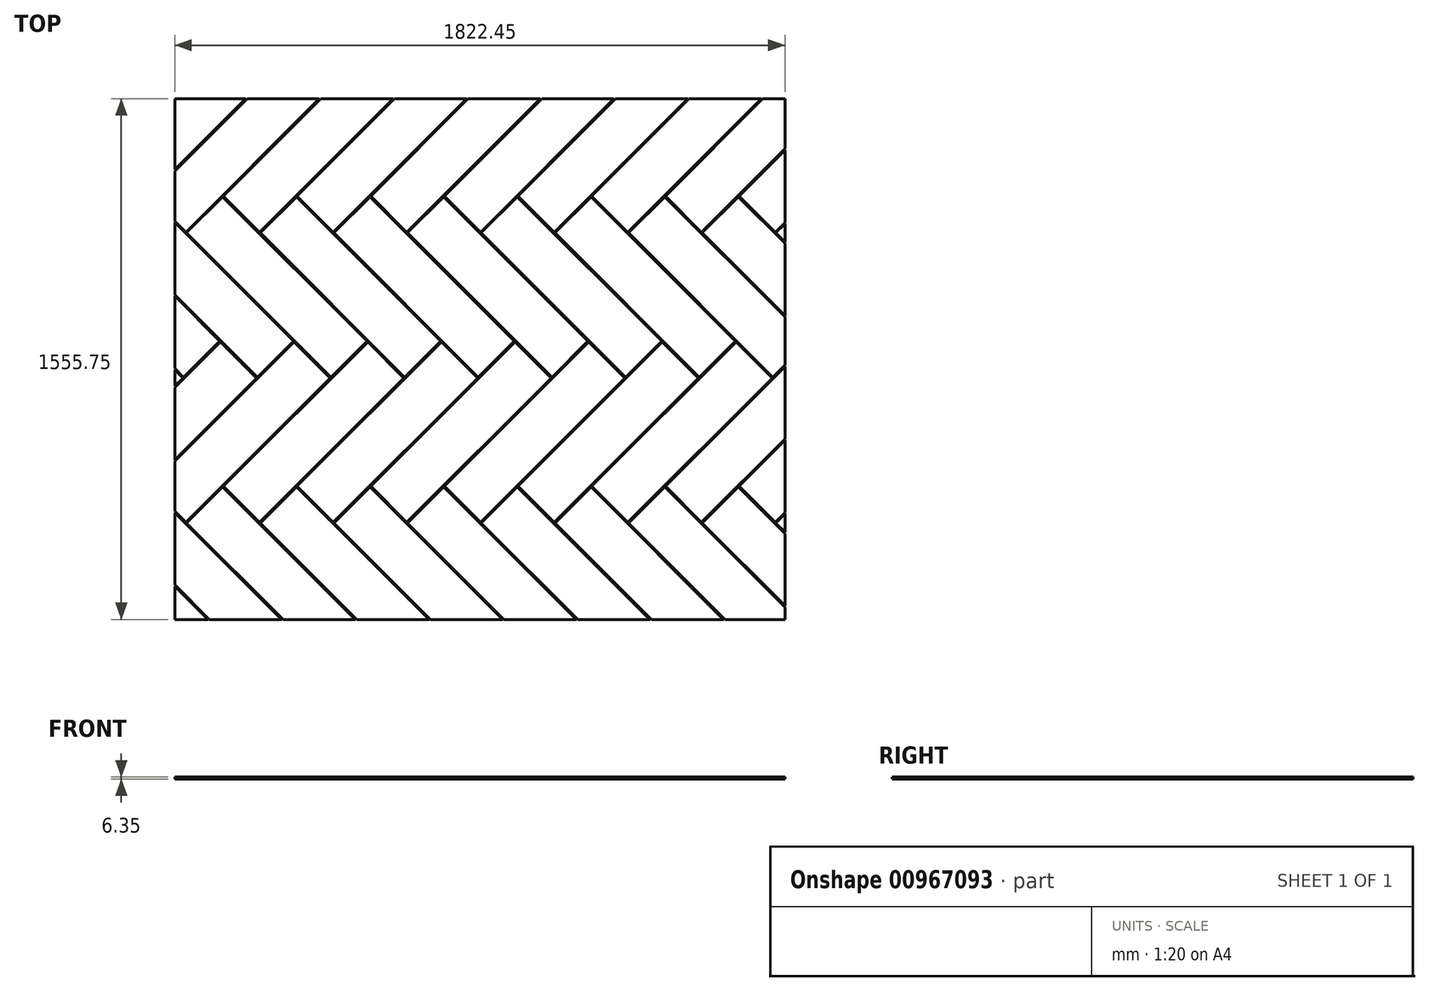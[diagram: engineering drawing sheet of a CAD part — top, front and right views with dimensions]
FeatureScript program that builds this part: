
annotation { "Feature Type Name" : "Feature", "Feature Type Description" : "" }
export const myFeature = defineFeature(function(context is Context, id is Id, definition is map)
    precondition{}
    {
        {
            var Q0;
            Q0=qCreatedBy(makeId("Top.planeOp"),FACE);
            var sketch = newSketch(context, id + "F0", { "sketchPlane" : qUnion([Q0])});
            skLineSegment(sketch, "E0.bottom", {"start": v(0, 0) * mm, "end": v(609.6, 0) * mm});
            skLineSegment(sketch, "E0.top", {"start": v(0, 152.4) * mm, "end": v(609.6, 152.4) * mm});
            skLineSegment(sketch, "E0.left", {"start": v(0, 0) * mm, "end": v(0, 152.4) * mm});
            skLineSegment(sketch, "E0.right", {"start": v(609.6, 0) * mm, "end": v(609.6, 152.4) * mm});
            skLineSegment(sketch, "E1.bottom", {"start": v(152.4, 155.57) * mm, "end": v(152.4, 765.17) * mm});
            skLineSegment(sketch, "E1.top", {"start": v(0, 155.58) * mm, "end": v(0, 765.17) * mm});
            skLineSegment(sketch, "E1.left", {"start": v(152.4, 155.57) * mm, "end": v(0, 155.57) * mm});
            skLineSegment(sketch, "E1.right", {"start": v(152.4, 765.17) * mm, "end": v(0, 765.17) * mm});
            skLineSegment(sketch, "E2.bottom", {"start": v(155.58, 155.57) * mm, "end": v(765.17, 155.57) * mm});
            skLineSegment(sketch, "E2.top", {"start": v(155.58, 307.98) * mm, "end": v(765.17, 307.97) * mm});
            skLineSegment(sketch, "E2.left", {"start": v(155.58, 155.58) * mm, "end": v(155.58, 307.98) * mm});
            skLineSegment(sketch, "E2.right", {"start": v(765.17, 155.57) * mm, "end": v(765.17, 307.97) * mm});
            skLineSegment(sketch, "E3.bottom", {"start": v(307.98, 311.15) * mm, "end": v(307.98, 920.75) * mm});
            skLineSegment(sketch, "E3.top", {"start": v(155.58, 311.15) * mm, "end": v(155.58, 920.75) * mm});
            skLineSegment(sketch, "E3.left", {"start": v(307.98, 311.15) * mm, "end": v(155.58, 311.15) * mm});
            skLineSegment(sketch, "E3.right", {"start": v(307.98, 920.75) * mm, "end": v(155.58, 920.75) * mm});
            skLineSegment(sketch, "E4.0.1.0", {"start": v(-612.78, 612.78) * mm, "end": v(-3.18, 612.78) * mm});
            skLineSegment(sketch, "E4.0.1.1", {"start": v(-460.37, 768.35) * mm, "end": v(-612.77, 768.35) * mm});
            skLineSegment(sketch, "E4.0.1.2", {"start": v(-457.2, 768.35) * mm, "end": v(-457.2, 920.75) * mm});
            skLineSegment(sketch, "E4.0.1.3", {"start": v(-304.8, 923.92) * mm, "end": v(-457.2, 923.92) * mm});
            skLineSegment(sketch, "E4.0.1.4", {"start": v(-457.2, 768.35) * mm, "end": v(152.4, 768.35) * mm});
            skLineSegment(sketch, "E4.0.1.5", {"start": v(-460.37, 768.35) * mm, "end": v(-460.37, 1377.95) * mm});
            skLineSegment(sketch, "E4.0.1.6", {"start": v(-457.2, 920.75) * mm, "end": v(152.4, 920.75) * mm});
            skLineSegment(sketch, "E4.0.1.7", {"start": v(-304.8, 1533.52) * mm, "end": v(-457.2, 1533.52) * mm});
            skLineSegment(sketch, "E4.0.1.8", {"start": v(-612.78, 768.35) * mm, "end": v(-612.77, 1377.95) * mm});
            skLineSegment(sketch, "E4.0.1.9", {"start": v(-457.2, 923.92) * mm, "end": v(-457.2, 1533.52) * mm});
            skLineSegment(sketch, "E4.0.1.10", {"start": v(-3.18, 612.78) * mm, "end": v(-3.18, 765.17) * mm});
            skLineSegment(sketch, "E4.0.1.11", {"start": v(-304.8, 923.92) * mm, "end": v(-304.8, 1533.52) * mm});
            skLineSegment(sketch, "E4.0.1.12", {"start": v(-612.78, 612.78) * mm, "end": v(-612.78, 765.17) * mm});
            skLineSegment(sketch, "E4.0.1.13", {"start": v(-460.37, 1377.95) * mm, "end": v(-612.77, 1377.95) * mm});
            skLineSegment(sketch, "E4.0.1.14", {"start": v(152.4, 768.35) * mm, "end": v(152.4, 920.75) * mm});
            skLineSegment(sketch, "E4.0.1.15", {"start": v(-612.77, 765.17) * mm, "end": v(-3.17, 765.17) * mm});
            skLineSegment(sketch, "E4.1.0.0", {"start": v(311.15, 311.15) * mm, "end": v(920.75, 311.15) * mm});
            skLineSegment(sketch, "E4.1.0.1", {"start": v(463.55, 466.72) * mm, "end": v(311.15, 466.72) * mm});
            skLineSegment(sketch, "E4.1.0.2", {"start": v(466.73, 466.72) * mm, "end": v(466.73, 619.12) * mm});
            skLineSegment(sketch, "E4.1.0.3", {"start": v(619.13, 622.3) * mm, "end": v(466.73, 622.3) * mm});
            skLineSegment(sketch, "E4.1.0.4", {"start": v(466.73, 466.72) * mm, "end": v(1076.33, 466.72) * mm});
            skLineSegment(sketch, "E4.1.0.5", {"start": v(463.55, 466.72) * mm, "end": v(463.55, 1076.32) * mm});
            skLineSegment(sketch, "E4.1.0.6", {"start": v(466.73, 619.12) * mm, "end": v(1076.33, 619.12) * mm});
            skLineSegment(sketch, "E4.1.0.7", {"start": v(619.13, 1231.9) * mm, "end": v(466.73, 1231.9) * mm});
            skLineSegment(sketch, "E4.1.0.8", {"start": v(311.15, 466.72) * mm, "end": v(311.15, 1076.32) * mm});
            skLineSegment(sketch, "E4.1.0.9", {"start": v(466.73, 622.3) * mm, "end": v(466.73, 1231.9) * mm});
            skLineSegment(sketch, "E4.1.0.10", {"start": v(920.75, 311.15) * mm, "end": v(920.75, 463.55) * mm});
            skLineSegment(sketch, "E4.1.0.11", {"start": v(619.13, 622.3) * mm, "end": v(619.13, 1231.9) * mm});
            skLineSegment(sketch, "E4.1.0.12", {"start": v(311.15, 311.15) * mm, "end": v(311.15, 463.55) * mm});
            skLineSegment(sketch, "E4.1.0.13", {"start": v(463.55, 1076.32) * mm, "end": v(311.15, 1076.32) * mm});
            skLineSegment(sketch, "E4.1.0.14", {"start": v(1076.32, 466.72) * mm, "end": v(1076.32, 619.12) * mm});
            skLineSegment(sketch, "E4.1.0.15", {"start": v(311.15, 463.55) * mm, "end": v(920.75, 463.55) * mm});
            skLineSegment(sketch, "E4.1.1.0", {"start": v(-301.62, 923.92) * mm, "end": v(307.98, 923.92) * mm});
            skLineSegment(sketch, "E4.1.1.1", {"start": v(-149.22, 1079.5) * mm, "end": v(-301.62, 1079.5) * mm});
            skLineSegment(sketch, "E4.1.1.2", {"start": v(-146.05, 1079.5) * mm, "end": v(-146.05, 1231.9) * mm});
            skLineSegment(sketch, "E4.1.1.3", {"start": v(6.35, 1235.07) * mm, "end": v(-146.05, 1235.07) * mm});
            skLineSegment(sketch, "E4.1.1.4", {"start": v(-146.05, 1079.5) * mm, "end": v(463.55, 1079.5) * mm});
            skLineSegment(sketch, "E4.1.1.5", {"start": v(-149.22, 1079.5) * mm, "end": v(-149.22, 1689.1) * mm});
            skLineSegment(sketch, "E4.1.1.6", {"start": v(-146.05, 1231.9) * mm, "end": v(463.55, 1231.9) * mm});
            skLineSegment(sketch, "E4.1.1.7", {"start": v(6.35, 1844.67) * mm, "end": v(-146.05, 1844.67) * mm});
            skLineSegment(sketch, "E4.1.1.8", {"start": v(-301.62, 1079.5) * mm, "end": v(-301.62, 1689.1) * mm});
            skLineSegment(sketch, "E4.1.1.9", {"start": v(-146.05, 1235.07) * mm, "end": v(-146.05, 1844.67) * mm});
            skLineSegment(sketch, "E4.1.1.10", {"start": v(307.98, 923.92) * mm, "end": v(307.98, 1076.32) * mm});
            skLineSegment(sketch, "E4.1.1.11", {"start": v(6.35, 1235.07) * mm, "end": v(6.35, 1844.67) * mm});
            skLineSegment(sketch, "E4.1.1.12", {"start": v(-301.62, 923.92) * mm, "end": v(-301.62, 1076.32) * mm});
            skLineSegment(sketch, "E4.1.1.13", {"start": v(-149.22, 1689.1) * mm, "end": v(-301.62, 1689.1) * mm});
            skLineSegment(sketch, "E4.1.1.14", {"start": v(463.55, 1079.5) * mm, "end": v(463.55, 1231.9) * mm});
            skLineSegment(sketch, "E4.1.1.15", {"start": v(-301.62, 1076.32) * mm, "end": v(307.98, 1076.32) * mm});
            skLineSegment(sketch, "E4.2.0.0", {"start": v(622.3, 622.3) * mm, "end": v(1231.9, 622.3) * mm});
            skLineSegment(sketch, "E4.2.0.1", {"start": v(774.7, 777.87) * mm, "end": v(622.3, 777.87) * mm});
            skLineSegment(sketch, "E4.2.0.2", {"start": v(777.88, 777.87) * mm, "end": v(777.88, 930.27) * mm});
            skLineSegment(sketch, "E4.2.0.3", {"start": v(930.28, 933.45) * mm, "end": v(777.88, 933.45) * mm});
            skLineSegment(sketch, "E4.2.0.4", {"start": v(777.88, 777.87) * mm, "end": v(1387.47, 777.87) * mm});
            skLineSegment(sketch, "E4.2.0.5", {"start": v(774.7, 777.87) * mm, "end": v(774.7, 1387.47) * mm});
            skLineSegment(sketch, "E4.2.0.6", {"start": v(777.88, 930.27) * mm, "end": v(1387.47, 930.27) * mm});
            skLineSegment(sketch, "E4.2.0.7", {"start": v(930.28, 1543.05) * mm, "end": v(777.88, 1543.05) * mm});
            skLineSegment(sketch, "E4.2.0.8", {"start": v(622.3, 777.87) * mm, "end": v(622.3, 1387.47) * mm});
            skLineSegment(sketch, "E4.2.0.9", {"start": v(777.88, 933.45) * mm, "end": v(777.88, 1543.05) * mm});
            skLineSegment(sketch, "E4.2.0.10", {"start": v(1231.9, 622.3) * mm, "end": v(1231.9, 774.7) * mm});
            skLineSegment(sketch, "E4.2.0.11", {"start": v(930.28, 933.45) * mm, "end": v(930.28, 1543.05) * mm});
            skLineSegment(sketch, "E4.2.0.12", {"start": v(622.3, 622.3) * mm, "end": v(622.3, 774.7) * mm});
            skLineSegment(sketch, "E4.2.0.13", {"start": v(774.7, 1387.47) * mm, "end": v(622.3, 1387.47) * mm});
            skLineSegment(sketch, "E4.2.0.14", {"start": v(1387.47, 777.87) * mm, "end": v(1387.47, 930.27) * mm});
            skLineSegment(sketch, "E4.2.0.15", {"start": v(622.3, 774.7) * mm, "end": v(1231.9, 774.7) * mm});
            skLineSegment(sketch, "E4.2.1.0", {"start": v(9.53, 1235.07) * mm, "end": v(619.13, 1235.07) * mm});
            skLineSegment(sketch, "E4.2.1.1", {"start": v(161.93, 1390.65) * mm, "end": v(9.53, 1390.65) * mm});
            skLineSegment(sketch, "E4.2.1.2", {"start": v(165.1, 1390.65) * mm, "end": v(165.1, 1543.05) * mm});
            skLineSegment(sketch, "E4.2.1.3", {"start": v(317.5, 1546.22) * mm, "end": v(165.1, 1546.22) * mm});
            skLineSegment(sketch, "E4.2.1.4", {"start": v(165.1, 1390.65) * mm, "end": v(774.7, 1390.65) * mm});
            skLineSegment(sketch, "E4.2.1.5", {"start": v(161.93, 1390.65) * mm, "end": v(161.93, 2000.25) * mm});
            skLineSegment(sketch, "E4.2.1.6", {"start": v(165.1, 1543.05) * mm, "end": v(774.7, 1543.05) * mm});
            skLineSegment(sketch, "E4.2.1.7", {"start": v(317.5, 2155.82) * mm, "end": v(165.1, 2155.82) * mm});
            skLineSegment(sketch, "E4.2.1.8", {"start": v(9.53, 1390.65) * mm, "end": v(9.53, 2000.25) * mm});
            skLineSegment(sketch, "E4.2.1.9", {"start": v(165.1, 1546.22) * mm, "end": v(165.1, 2155.82) * mm});
            skLineSegment(sketch, "E4.2.1.10", {"start": v(619.13, 1235.07) * mm, "end": v(619.13, 1387.47) * mm});
            skLineSegment(sketch, "E4.2.1.11", {"start": v(317.5, 1546.22) * mm, "end": v(317.5, 2155.82) * mm});
            skLineSegment(sketch, "E4.2.1.12", {"start": v(9.53, 1235.07) * mm, "end": v(9.53, 1387.47) * mm});
            skLineSegment(sketch, "E4.2.1.13", {"start": v(161.93, 2000.25) * mm, "end": v(9.53, 2000.25) * mm});
            skLineSegment(sketch, "E4.2.1.14", {"start": v(774.7, 1390.65) * mm, "end": v(774.7, 1543.05) * mm});
            skLineSegment(sketch, "E4.2.1.15", {"start": v(9.53, 1387.47) * mm, "end": v(619.13, 1387.47) * mm});
            skLineSegment(sketch, "E4.direction1", {"start": v(0, 0) * mm, "end": v(311.15, 311.15) * mm, "construction": true});
            skLineSegment(sketch, "E4.direction2", {"start": v(0, 0) * mm, "end": v(-612.78, 612.78) * mm, "construction": true});
            skLineSegment(sketch, "E5.0.3.0", {"start": v(933.45, 933.45) * mm, "end": v(1543.05, 933.45) * mm});
            skLineSegment(sketch, "E5.3.3.0", {"start": v(1085.85, 1089.02) * mm, "end": v(933.45, 1089.02) * mm});
            skLineSegment(sketch, "E5.6.3.0", {"start": v(1089.03, 1089.02) * mm, "end": v(1089.03, 1241.42) * mm});
            skLineSegment(sketch, "E5.9.3.0", {"start": v(1241.43, 1244.6) * mm, "end": v(1089.03, 1244.6) * mm});
            skLineSegment(sketch, "E5.12.3.0", {"start": v(1089.03, 1089.02) * mm, "end": v(1698.62, 1089.02) * mm});
            skLineSegment(sketch, "E5.15.3.0", {"start": v(1085.85, 1089.02) * mm, "end": v(1085.85, 1698.62) * mm});
            skLineSegment(sketch, "E5.18.3.0", {"start": v(1089.03, 1241.42) * mm, "end": v(1698.62, 1241.42) * mm});
            skLineSegment(sketch, "E5.21.3.0", {"start": v(1241.43, 1854.2) * mm, "end": v(1089.03, 1854.2) * mm});
            skLineSegment(sketch, "E5.24.3.0", {"start": v(933.45, 1089.02) * mm, "end": v(933.45, 1698.62) * mm});
            skLineSegment(sketch, "E5.27.3.0", {"start": v(1089.03, 1244.6) * mm, "end": v(1089.03, 1854.2) * mm});
            skLineSegment(sketch, "E5.30.3.0", {"start": v(1543.05, 933.45) * mm, "end": v(1543.05, 1085.85) * mm});
            skLineSegment(sketch, "E5.33.3.0", {"start": v(1241.43, 1244.6) * mm, "end": v(1241.43, 1854.2) * mm});
            skLineSegment(sketch, "E5.36.3.0", {"start": v(933.45, 933.45) * mm, "end": v(933.45, 1085.85) * mm});
            skLineSegment(sketch, "E5.39.3.0", {"start": v(1085.85, 1698.62) * mm, "end": v(933.45, 1698.62) * mm});
            skLineSegment(sketch, "E5.42.3.0", {"start": v(1698.62, 1089.02) * mm, "end": v(1698.62, 1241.42) * mm});
            skLineSegment(sketch, "E5.45.3.0", {"start": v(933.45, 1085.85) * mm, "end": v(1543.05, 1085.85) * mm});
            skLineSegment(sketch, "E5.0.3.1", {"start": v(320.68, 1546.22) * mm, "end": v(930.28, 1546.22) * mm});
            skLineSegment(sketch, "E5.3.3.1", {"start": v(473.08, 1701.8) * mm, "end": v(320.68, 1701.8) * mm});
            skLineSegment(sketch, "E5.6.3.1", {"start": v(476.25, 1701.8) * mm, "end": v(476.25, 1854.2) * mm});
            skLineSegment(sketch, "E5.9.3.1", {"start": v(628.65, 1857.37) * mm, "end": v(476.25, 1857.37) * mm});
            skLineSegment(sketch, "E5.12.3.1", {"start": v(476.25, 1701.8) * mm, "end": v(1085.85, 1701.8) * mm});
            skLineSegment(sketch, "E5.15.3.1", {"start": v(473.08, 1701.8) * mm, "end": v(473.08, 2311.4) * mm});
            skLineSegment(sketch, "E5.18.3.1", {"start": v(476.25, 1854.2) * mm, "end": v(1085.85, 1854.2) * mm});
            skLineSegment(sketch, "E5.21.3.1", {"start": v(628.65, 2466.97) * mm, "end": v(476.25, 2466.97) * mm});
            skLineSegment(sketch, "E5.24.3.1", {"start": v(320.68, 1701.8) * mm, "end": v(320.68, 2311.4) * mm});
            skLineSegment(sketch, "E5.27.3.1", {"start": v(476.25, 1857.37) * mm, "end": v(476.25, 2466.97) * mm});
            skLineSegment(sketch, "E5.30.3.1", {"start": v(930.28, 1546.22) * mm, "end": v(930.28, 1698.62) * mm});
            skLineSegment(sketch, "E5.33.3.1", {"start": v(628.65, 1857.37) * mm, "end": v(628.65, 2466.97) * mm});
            skLineSegment(sketch, "E5.36.3.1", {"start": v(320.68, 1546.22) * mm, "end": v(320.68, 1698.62) * mm});
            skLineSegment(sketch, "E5.39.3.1", {"start": v(473.08, 2311.4) * mm, "end": v(320.68, 2311.4) * mm});
            skLineSegment(sketch, "E5.42.3.1", {"start": v(1085.85, 1701.8) * mm, "end": v(1085.85, 1854.2) * mm});
            skLineSegment(sketch, "E5.45.3.1", {"start": v(320.68, 1698.62) * mm, "end": v(930.28, 1698.62) * mm});
            skLineSegment(sketch, "E5.0.4.0", {"start": v(1244.6, 1244.6) * mm, "end": v(1854.2, 1244.6) * mm});
            skLineSegment(sketch, "E5.3.4.0", {"start": v(1397, 1400.17) * mm, "end": v(1244.6, 1400.17) * mm});
            skLineSegment(sketch, "E5.6.4.0", {"start": v(1400.18, 1400.17) * mm, "end": v(1400.18, 1552.57) * mm});
            skLineSegment(sketch, "E5.9.4.0", {"start": v(1552.58, 1555.75) * mm, "end": v(1400.18, 1555.75) * mm});
            skLineSegment(sketch, "E5.12.4.0", {"start": v(1400.18, 1400.17) * mm, "end": v(2009.78, 1400.17) * mm});
            skLineSegment(sketch, "E5.15.4.0", {"start": v(1397, 1400.17) * mm, "end": v(1397, 2009.77) * mm});
            skLineSegment(sketch, "E5.18.4.0", {"start": v(1400.18, 1552.57) * mm, "end": v(2009.78, 1552.57) * mm});
            skLineSegment(sketch, "E5.21.4.0", {"start": v(1552.58, 2165.35) * mm, "end": v(1400.18, 2165.35) * mm});
            skLineSegment(sketch, "E5.24.4.0", {"start": v(1244.6, 1400.17) * mm, "end": v(1244.6, 2009.77) * mm});
            skLineSegment(sketch, "E5.27.4.0", {"start": v(1400.18, 1555.75) * mm, "end": v(1400.18, 2165.35) * mm});
            skLineSegment(sketch, "E5.30.4.0", {"start": v(1854.2, 1244.6) * mm, "end": v(1854.2, 1397) * mm});
            skLineSegment(sketch, "E5.33.4.0", {"start": v(1552.58, 1555.75) * mm, "end": v(1552.58, 2165.35) * mm});
            skLineSegment(sketch, "E5.36.4.0", {"start": v(1244.6, 1244.6) * mm, "end": v(1244.6, 1397) * mm});
            skLineSegment(sketch, "E5.39.4.0", {"start": v(1397, 2009.77) * mm, "end": v(1244.6, 2009.77) * mm});
            skLineSegment(sketch, "E5.42.4.0", {"start": v(2009.78, 1400.17) * mm, "end": v(2009.78, 1552.57) * mm});
            skLineSegment(sketch, "E5.45.4.0", {"start": v(1244.6, 1397) * mm, "end": v(1854.2, 1397) * mm});
            skLineSegment(sketch, "E5.0.4.1", {"start": v(631.83, 1857.37) * mm, "end": v(1241.43, 1857.37) * mm});
            skLineSegment(sketch, "E5.3.4.1", {"start": v(784.23, 2012.95) * mm, "end": v(631.83, 2012.95) * mm});
            skLineSegment(sketch, "E5.6.4.1", {"start": v(787.4, 2012.95) * mm, "end": v(787.4, 2165.35) * mm});
            skLineSegment(sketch, "E5.9.4.1", {"start": v(939.8, 2168.52) * mm, "end": v(787.4, 2168.52) * mm});
            skLineSegment(sketch, "E5.12.4.1", {"start": v(787.4, 2012.95) * mm, "end": v(1397, 2012.95) * mm});
            skLineSegment(sketch, "E5.15.4.1", {"start": v(784.23, 2012.95) * mm, "end": v(784.23, 2622.55) * mm});
            skLineSegment(sketch, "E5.18.4.1", {"start": v(787.4, 2165.35) * mm, "end": v(1397, 2165.35) * mm});
            skLineSegment(sketch, "E5.21.4.1", {"start": v(939.8, 2778.12) * mm, "end": v(787.4, 2778.12) * mm});
            skLineSegment(sketch, "E5.24.4.1", {"start": v(631.83, 2012.95) * mm, "end": v(631.83, 2622.55) * mm});
            skLineSegment(sketch, "E5.27.4.1", {"start": v(787.4, 2168.52) * mm, "end": v(787.4, 2778.12) * mm});
            skLineSegment(sketch, "E5.30.4.1", {"start": v(1241.43, 1857.37) * mm, "end": v(1241.43, 2009.77) * mm});
            skLineSegment(sketch, "E5.33.4.1", {"start": v(939.8, 2168.52) * mm, "end": v(939.8, 2778.12) * mm});
            skLineSegment(sketch, "E5.36.4.1", {"start": v(631.83, 1857.37) * mm, "end": v(631.83, 2009.77) * mm});
            skLineSegment(sketch, "E5.39.4.1", {"start": v(784.23, 2622.55) * mm, "end": v(631.83, 2622.55) * mm});
            skLineSegment(sketch, "E5.42.4.1", {"start": v(1397, 2012.95) * mm, "end": v(1397, 2165.35) * mm});
            skLineSegment(sketch, "E5.45.4.1", {"start": v(631.83, 2009.77) * mm, "end": v(1241.43, 2009.77) * mm});
            skLineSegment(sketch, "E5.0.5.0", {"start": v(1555.75, 1555.75) * mm, "end": v(2165.35, 1555.75) * mm});
            skLineSegment(sketch, "E5.3.5.0", {"start": v(1708.15, 1711.32) * mm, "end": v(1555.75, 1711.32) * mm});
            skLineSegment(sketch, "E5.6.5.0", {"start": v(1711.33, 1711.32) * mm, "end": v(1711.33, 1863.72) * mm});
            skLineSegment(sketch, "E5.9.5.0", {"start": v(1863.73, 1866.9) * mm, "end": v(1711.33, 1866.9) * mm});
            skLineSegment(sketch, "E5.12.5.0", {"start": v(1711.33, 1711.32) * mm, "end": v(2320.92, 1711.32) * mm});
            skLineSegment(sketch, "E5.15.5.0", {"start": v(1708.15, 1711.32) * mm, "end": v(1708.15, 2320.92) * mm});
            skLineSegment(sketch, "E5.18.5.0", {"start": v(1711.33, 1863.72) * mm, "end": v(2320.92, 1863.72) * mm});
            skLineSegment(sketch, "E5.21.5.0", {"start": v(1863.73, 2476.5) * mm, "end": v(1711.33, 2476.5) * mm});
            skLineSegment(sketch, "E5.24.5.0", {"start": v(1555.75, 1711.32) * mm, "end": v(1555.75, 2320.92) * mm});
            skLineSegment(sketch, "E5.27.5.0", {"start": v(1711.33, 1866.9) * mm, "end": v(1711.33, 2476.5) * mm});
            skLineSegment(sketch, "E5.30.5.0", {"start": v(2165.35, 1555.75) * mm, "end": v(2165.35, 1708.15) * mm});
            skLineSegment(sketch, "E5.33.5.0", {"start": v(1863.73, 1866.9) * mm, "end": v(1863.73, 2476.5) * mm});
            skLineSegment(sketch, "E5.36.5.0", {"start": v(1555.75, 1555.75) * mm, "end": v(1555.75, 1708.15) * mm});
            skLineSegment(sketch, "E5.39.5.0", {"start": v(1708.15, 2320.92) * mm, "end": v(1555.75, 2320.92) * mm});
            skLineSegment(sketch, "E5.42.5.0", {"start": v(2320.92, 1711.32) * mm, "end": v(2320.92, 1863.72) * mm});
            skLineSegment(sketch, "E5.45.5.0", {"start": v(1555.75, 1708.15) * mm, "end": v(2165.35, 1708.15) * mm});
            skLineSegment(sketch, "E5.0.5.1", {"start": v(942.98, 2168.52) * mm, "end": v(1552.58, 2168.52) * mm});
            skLineSegment(sketch, "E5.3.5.1", {"start": v(1095.38, 2324.1) * mm, "end": v(942.98, 2324.1) * mm});
            skLineSegment(sketch, "E5.6.5.1", {"start": v(1098.55, 2324.1) * mm, "end": v(1098.55, 2476.5) * mm});
            skLineSegment(sketch, "E5.9.5.1", {"start": v(1250.95, 2479.67) * mm, "end": v(1098.55, 2479.67) * mm});
            skLineSegment(sketch, "E5.12.5.1", {"start": v(1098.55, 2324.1) * mm, "end": v(1708.15, 2324.1) * mm});
            skLineSegment(sketch, "E5.15.5.1", {"start": v(1095.38, 2324.1) * mm, "end": v(1095.38, 2933.7) * mm});
            skLineSegment(sketch, "E5.18.5.1", {"start": v(1098.55, 2476.5) * mm, "end": v(1708.15, 2476.5) * mm});
            skLineSegment(sketch, "E5.21.5.1", {"start": v(1250.95, 3089.27) * mm, "end": v(1098.55, 3089.27) * mm});
            skLineSegment(sketch, "E5.24.5.1", {"start": v(942.98, 2324.1) * mm, "end": v(942.98, 2933.7) * mm});
            skLineSegment(sketch, "E5.27.5.1", {"start": v(1098.55, 2479.67) * mm, "end": v(1098.55, 3089.27) * mm});
            skLineSegment(sketch, "E5.30.5.1", {"start": v(1552.58, 2168.52) * mm, "end": v(1552.58, 2320.92) * mm});
            skLineSegment(sketch, "E5.33.5.1", {"start": v(1250.95, 2479.67) * mm, "end": v(1250.95, 3089.27) * mm});
            skLineSegment(sketch, "E5.36.5.1", {"start": v(942.98, 2168.52) * mm, "end": v(942.98, 2320.92) * mm});
            skLineSegment(sketch, "E5.39.5.1", {"start": v(1095.38, 2933.7) * mm, "end": v(942.98, 2933.7) * mm});
            skLineSegment(sketch, "E5.42.5.1", {"start": v(1708.15, 2324.1) * mm, "end": v(1708.15, 2476.5) * mm});
            skLineSegment(sketch, "E5.45.5.1", {"start": v(942.98, 2320.92) * mm, "end": v(1552.58, 2320.92) * mm});
            skLineSegment(sketch, "E6.0.0.2", {"start": v(-1225.55, 1225.55) * mm, "end": v(-615.95, 1225.55) * mm});
            skLineSegment(sketch, "E6.3.0.2", {"start": v(-1073.15, 1381.12) * mm, "end": v(-1225.55, 1381.12) * mm});
            skLineSegment(sketch, "E6.6.0.2", {"start": v(-1069.97, 1381.12) * mm, "end": v(-1069.97, 1533.52) * mm});
            skLineSegment(sketch, "E6.9.0.2", {"start": v(-917.57, 1536.7) * mm, "end": v(-1069.97, 1536.7) * mm});
            skLineSegment(sketch, "E6.12.0.2", {"start": v(-1069.97, 1381.12) * mm, "end": v(-460.37, 1381.12) * mm});
            skLineSegment(sketch, "E6.15.0.2", {"start": v(-1073.15, 1381.12) * mm, "end": v(-1073.15, 1990.72) * mm});
            skLineSegment(sketch, "E6.18.0.2", {"start": v(-1069.97, 1533.52) * mm, "end": v(-460.37, 1533.52) * mm});
            skLineSegment(sketch, "E6.21.0.2", {"start": v(-917.57, 2146.3) * mm, "end": v(-1069.97, 2146.3) * mm});
            skLineSegment(sketch, "E6.24.0.2", {"start": v(-1225.55, 1381.12) * mm, "end": v(-1225.55, 1990.72) * mm});
            skLineSegment(sketch, "E6.27.0.2", {"start": v(-1069.97, 1536.7) * mm, "end": v(-1069.97, 2146.3) * mm});
            skLineSegment(sketch, "E6.30.0.2", {"start": v(-615.95, 1225.55) * mm, "end": v(-615.95, 1377.95) * mm});
            skLineSegment(sketch, "E6.33.0.2", {"start": v(-917.57, 1536.7) * mm, "end": v(-917.57, 2146.3) * mm});
            skLineSegment(sketch, "E6.36.0.2", {"start": v(-1225.55, 1225.55) * mm, "end": v(-1225.55, 1377.95) * mm});
            skLineSegment(sketch, "E6.39.0.2", {"start": v(-1073.15, 1990.72) * mm, "end": v(-1225.55, 1990.72) * mm});
            skLineSegment(sketch, "E6.42.0.2", {"start": v(-460.37, 1381.12) * mm, "end": v(-460.37, 1533.52) * mm});
            skLineSegment(sketch, "E6.45.0.2", {"start": v(-1225.55, 1377.95) * mm, "end": v(-615.95, 1377.95) * mm});
            skLineSegment(sketch, "E6.0.0.3", {"start": v(-1838.33, 1838.33) * mm, "end": v(-1228.73, 1838.33) * mm});
            skLineSegment(sketch, "E6.3.0.3", {"start": v(-1685.92, 1993.9) * mm, "end": v(-1838.32, 1993.9) * mm});
            skLineSegment(sketch, "E6.6.0.3", {"start": v(-1682.75, 1993.9) * mm, "end": v(-1682.75, 2146.3) * mm});
            skLineSegment(sketch, "E6.9.0.3", {"start": v(-1530.35, 2149.47) * mm, "end": v(-1682.75, 2149.47) * mm});
            skLineSegment(sketch, "E6.12.0.3", {"start": v(-1682.75, 1993.9) * mm, "end": v(-1073.15, 1993.9) * mm});
            skLineSegment(sketch, "E6.15.0.3", {"start": v(-1685.92, 1993.9) * mm, "end": v(-1685.92, 2603.5) * mm});
            skLineSegment(sketch, "E6.18.0.3", {"start": v(-1682.75, 2146.3) * mm, "end": v(-1073.15, 2146.3) * mm});
            skLineSegment(sketch, "E6.21.0.3", {"start": v(-1530.35, 2759.07) * mm, "end": v(-1682.75, 2759.07) * mm});
            skLineSegment(sketch, "E6.24.0.3", {"start": v(-1838.33, 1993.9) * mm, "end": v(-1838.33, 2603.5) * mm});
            skLineSegment(sketch, "E6.27.0.3", {"start": v(-1682.75, 2149.47) * mm, "end": v(-1682.75, 2759.07) * mm});
            skLineSegment(sketch, "E6.30.0.3", {"start": v(-1228.73, 1838.33) * mm, "end": v(-1228.73, 1990.72) * mm});
            skLineSegment(sketch, "E6.33.0.3", {"start": v(-1530.35, 2149.47) * mm, "end": v(-1530.35, 2759.07) * mm});
            skLineSegment(sketch, "E6.36.0.3", {"start": v(-1838.33, 1838.33) * mm, "end": v(-1838.33, 1990.72) * mm});
            skLineSegment(sketch, "E6.39.0.3", {"start": v(-1685.92, 2603.5) * mm, "end": v(-1838.32, 2603.5) * mm});
            skLineSegment(sketch, "E6.42.0.3", {"start": v(-1073.15, 1993.9) * mm, "end": v(-1073.15, 2146.3) * mm});
            skLineSegment(sketch, "E6.45.0.3", {"start": v(-1838.32, 1990.72) * mm, "end": v(-1228.72, 1990.72) * mm});
            skLineSegment(sketch, "E6.0.0.4", {"start": v(-2451.1, 2451.1) * mm, "end": v(-1841.5, 2451.1) * mm});
            skLineSegment(sketch, "E6.3.0.4", {"start": v(-2298.7, 2606.67) * mm, "end": v(-2451.1, 2606.67) * mm});
            skLineSegment(sketch, "E6.6.0.4", {"start": v(-2295.52, 2606.67) * mm, "end": v(-2295.52, 2759.07) * mm});
            skLineSegment(sketch, "E6.9.0.4", {"start": v(-2143.12, 2762.25) * mm, "end": v(-2295.52, 2762.25) * mm});
            skLineSegment(sketch, "E6.12.0.4", {"start": v(-2295.52, 2606.67) * mm, "end": v(-1685.92, 2606.67) * mm});
            skLineSegment(sketch, "E6.15.0.4", {"start": v(-2298.7, 2606.67) * mm, "end": v(-2298.7, 3216.27) * mm});
            skLineSegment(sketch, "E6.18.0.4", {"start": v(-2295.52, 2759.07) * mm, "end": v(-1685.92, 2759.07) * mm});
            skLineSegment(sketch, "E6.21.0.4", {"start": v(-2143.12, 3371.85) * mm, "end": v(-2295.52, 3371.85) * mm});
            skLineSegment(sketch, "E6.24.0.4", {"start": v(-2451.1, 2606.67) * mm, "end": v(-2451.1, 3216.27) * mm});
            skLineSegment(sketch, "E6.27.0.4", {"start": v(-2295.52, 2762.25) * mm, "end": v(-2295.52, 3371.85) * mm});
            skLineSegment(sketch, "E6.30.0.4", {"start": v(-1841.5, 2451.1) * mm, "end": v(-1841.5, 2603.5) * mm});
            skLineSegment(sketch, "E6.33.0.4", {"start": v(-2143.12, 2762.25) * mm, "end": v(-2143.12, 3371.85) * mm});
            skLineSegment(sketch, "E6.36.0.4", {"start": v(-2451.1, 2451.1) * mm, "end": v(-2451.1, 2603.5) * mm});
            skLineSegment(sketch, "E6.39.0.4", {"start": v(-2298.7, 3216.27) * mm, "end": v(-2451.1, 3216.27) * mm});
            skLineSegment(sketch, "E6.42.0.4", {"start": v(-1685.92, 2606.67) * mm, "end": v(-1685.92, 2759.07) * mm});
            skLineSegment(sketch, "E6.45.0.4", {"start": v(-2451.1, 2603.5) * mm, "end": v(-1841.5, 2603.5) * mm});
            skLineSegment(sketch, "E6.0.1.2", {"start": v(-914.4, 1536.7) * mm, "end": v(-304.8, 1536.7) * mm});
            skLineSegment(sketch, "E6.3.1.2", {"start": v(-762, 1692.27) * mm, "end": v(-914.4, 1692.27) * mm});
            skLineSegment(sketch, "E6.6.1.2", {"start": v(-758.82, 1692.27) * mm, "end": v(-758.82, 1844.67) * mm});
            skLineSegment(sketch, "E6.9.1.2", {"start": v(-606.42, 1847.85) * mm, "end": v(-758.82, 1847.85) * mm});
            skLineSegment(sketch, "E6.12.1.2", {"start": v(-758.82, 1692.27) * mm, "end": v(-149.22, 1692.27) * mm});
            skLineSegment(sketch, "E6.15.1.2", {"start": v(-762, 1692.27) * mm, "end": v(-762, 2301.87) * mm});
            skLineSegment(sketch, "E6.18.1.2", {"start": v(-758.82, 1844.67) * mm, "end": v(-149.22, 1844.67) * mm});
            skLineSegment(sketch, "E6.21.1.2", {"start": v(-606.42, 2457.45) * mm, "end": v(-758.82, 2457.45) * mm});
            skLineSegment(sketch, "E6.24.1.2", {"start": v(-914.4, 1692.27) * mm, "end": v(-914.4, 2301.87) * mm});
            skLineSegment(sketch, "E6.27.1.2", {"start": v(-758.82, 1847.85) * mm, "end": v(-758.82, 2457.45) * mm});
            skLineSegment(sketch, "E6.30.1.2", {"start": v(-304.8, 1536.7) * mm, "end": v(-304.8, 1689.1) * mm});
            skLineSegment(sketch, "E6.33.1.2", {"start": v(-606.42, 1847.85) * mm, "end": v(-606.42, 2457.45) * mm});
            skLineSegment(sketch, "E6.36.1.2", {"start": v(-914.4, 1536.7) * mm, "end": v(-914.4, 1689.1) * mm});
            skLineSegment(sketch, "E6.39.1.2", {"start": v(-762, 2301.87) * mm, "end": v(-914.4, 2301.87) * mm});
            skLineSegment(sketch, "E6.42.1.2", {"start": v(-149.22, 1692.27) * mm, "end": v(-149.22, 1844.67) * mm});
            skLineSegment(sketch, "E6.45.1.2", {"start": v(-914.4, 1689.1) * mm, "end": v(-304.8, 1689.1) * mm});
            skLineSegment(sketch, "E6.0.1.3", {"start": v(-1527.17, 2149.47) * mm, "end": v(-917.57, 2149.47) * mm});
            skLineSegment(sketch, "E6.3.1.3", {"start": v(-1374.77, 2305.05) * mm, "end": v(-1527.17, 2305.05) * mm});
            skLineSegment(sketch, "E6.6.1.3", {"start": v(-1371.6, 2305.05) * mm, "end": v(-1371.6, 2457.45) * mm});
            skLineSegment(sketch, "E6.9.1.3", {"start": v(-1219.2, 2460.62) * mm, "end": v(-1371.6, 2460.62) * mm});
            skLineSegment(sketch, "E6.12.1.3", {"start": v(-1371.6, 2305.05) * mm, "end": v(-762, 2305.05) * mm});
            skLineSegment(sketch, "E6.15.1.3", {"start": v(-1374.77, 2305.05) * mm, "end": v(-1374.77, 2914.65) * mm});
            skLineSegment(sketch, "E6.18.1.3", {"start": v(-1371.6, 2457.45) * mm, "end": v(-762, 2457.45) * mm});
            skLineSegment(sketch, "E6.21.1.3", {"start": v(-1219.2, 3070.22) * mm, "end": v(-1371.6, 3070.22) * mm});
            skLineSegment(sketch, "E6.24.1.3", {"start": v(-1527.17, 2305.05) * mm, "end": v(-1527.17, 2914.65) * mm});
            skLineSegment(sketch, "E6.27.1.3", {"start": v(-1371.6, 2460.62) * mm, "end": v(-1371.6, 3070.22) * mm});
            skLineSegment(sketch, "E6.30.1.3", {"start": v(-917.57, 2149.47) * mm, "end": v(-917.57, 2301.87) * mm});
            skLineSegment(sketch, "E6.33.1.3", {"start": v(-1219.2, 2460.62) * mm, "end": v(-1219.2, 3070.22) * mm});
            skLineSegment(sketch, "E6.36.1.3", {"start": v(-1527.17, 2149.47) * mm, "end": v(-1527.17, 2301.87) * mm});
            skLineSegment(sketch, "E6.39.1.3", {"start": v(-1374.77, 2914.65) * mm, "end": v(-1527.17, 2914.65) * mm});
            skLineSegment(sketch, "E6.42.1.3", {"start": v(-762, 2305.05) * mm, "end": v(-762, 2457.45) * mm});
            skLineSegment(sketch, "E6.45.1.3", {"start": v(-1527.17, 2301.87) * mm, "end": v(-917.57, 2301.87) * mm});
            skLineSegment(sketch, "E6.0.1.4", {"start": v(-2139.95, 2762.25) * mm, "end": v(-1530.35, 2762.25) * mm});
            skLineSegment(sketch, "E6.3.1.4", {"start": v(-1987.55, 2917.82) * mm, "end": v(-2139.95, 2917.82) * mm});
            skLineSegment(sketch, "E6.6.1.4", {"start": v(-1984.37, 2917.82) * mm, "end": v(-1984.37, 3070.22) * mm});
            skLineSegment(sketch, "E6.9.1.4", {"start": v(-1831.97, 3073.4) * mm, "end": v(-1984.37, 3073.4) * mm});
            skLineSegment(sketch, "E6.12.1.4", {"start": v(-1984.37, 2917.82) * mm, "end": v(-1374.77, 2917.82) * mm});
            skLineSegment(sketch, "E6.15.1.4", {"start": v(-1987.55, 2917.82) * mm, "end": v(-1987.55, 3527.42) * mm});
            skLineSegment(sketch, "E6.18.1.4", {"start": v(-1984.37, 3070.22) * mm, "end": v(-1374.77, 3070.22) * mm});
            skLineSegment(sketch, "E6.21.1.4", {"start": v(-1831.97, 3683) * mm, "end": v(-1984.37, 3683) * mm});
            skLineSegment(sketch, "E6.24.1.4", {"start": v(-2139.95, 2917.82) * mm, "end": v(-2139.95, 3527.42) * mm});
            skLineSegment(sketch, "E6.27.1.4", {"start": v(-1984.37, 3073.4) * mm, "end": v(-1984.37, 3683) * mm});
            skLineSegment(sketch, "E6.30.1.4", {"start": v(-1530.35, 2762.25) * mm, "end": v(-1530.35, 2914.65) * mm});
            skLineSegment(sketch, "E6.33.1.4", {"start": v(-1831.97, 3073.4) * mm, "end": v(-1831.97, 3683) * mm});
            skLineSegment(sketch, "E6.36.1.4", {"start": v(-2139.95, 2762.25) * mm, "end": v(-2139.95, 2914.65) * mm});
            skLineSegment(sketch, "E6.39.1.4", {"start": v(-1987.55, 3527.42) * mm, "end": v(-2139.95, 3527.42) * mm});
            skLineSegment(sketch, "E6.42.1.4", {"start": v(-1374.77, 2917.82) * mm, "end": v(-1374.77, 3070.22) * mm});
            skLineSegment(sketch, "E6.45.1.4", {"start": v(-2139.95, 2914.65) * mm, "end": v(-1530.35, 2914.65) * mm});
            skLineSegment(sketch, "E6.0.2.2", {"start": v(-603.25, 1847.85) * mm, "end": v(6.35, 1847.85) * mm});
            skLineSegment(sketch, "E6.3.2.2", {"start": v(-450.85, 2003.42) * mm, "end": v(-603.25, 2003.42) * mm});
            skLineSegment(sketch, "E6.6.2.2", {"start": v(-447.67, 2003.42) * mm, "end": v(-447.67, 2155.82) * mm});
            skLineSegment(sketch, "E6.9.2.2", {"start": v(-295.27, 2159) * mm, "end": v(-447.67, 2159) * mm});
            skLineSegment(sketch, "E6.12.2.2", {"start": v(-447.67, 2003.42) * mm, "end": v(161.93, 2003.42) * mm});
            skLineSegment(sketch, "E6.15.2.2", {"start": v(-450.85, 2003.42) * mm, "end": v(-450.85, 2613.02) * mm});
            skLineSegment(sketch, "E6.18.2.2", {"start": v(-447.67, 2155.82) * mm, "end": v(161.93, 2155.82) * mm});
            skLineSegment(sketch, "E6.21.2.2", {"start": v(-295.27, 2768.6) * mm, "end": v(-447.67, 2768.6) * mm});
            skLineSegment(sketch, "E6.24.2.2", {"start": v(-603.25, 2003.42) * mm, "end": v(-603.25, 2613.02) * mm});
            skLineSegment(sketch, "E6.27.2.2", {"start": v(-447.67, 2159) * mm, "end": v(-447.67, 2768.6) * mm});
            skLineSegment(sketch, "E6.30.2.2", {"start": v(6.35, 1847.85) * mm, "end": v(6.35, 2000.25) * mm});
            skLineSegment(sketch, "E6.33.2.2", {"start": v(-295.27, 2159) * mm, "end": v(-295.27, 2768.6) * mm});
            skLineSegment(sketch, "E6.36.2.2", {"start": v(-603.25, 1847.85) * mm, "end": v(-603.25, 2000.25) * mm});
            skLineSegment(sketch, "E6.39.2.2", {"start": v(-450.85, 2613.02) * mm, "end": v(-603.25, 2613.02) * mm});
            skLineSegment(sketch, "E6.42.2.2", {"start": v(161.93, 2003.42) * mm, "end": v(161.93, 2155.82) * mm});
            skLineSegment(sketch, "E6.45.2.2", {"start": v(-603.25, 2000.25) * mm, "end": v(6.35, 2000.25) * mm});
            skLineSegment(sketch, "E6.0.2.3", {"start": v(-1216.02, 2460.62) * mm, "end": v(-606.42, 2460.62) * mm});
            skLineSegment(sketch, "E6.3.2.3", {"start": v(-1063.62, 2616.2) * mm, "end": v(-1216.02, 2616.2) * mm});
            skLineSegment(sketch, "E6.6.2.3", {"start": v(-1060.45, 2616.2) * mm, "end": v(-1060.45, 2768.6) * mm});
            skLineSegment(sketch, "E6.9.2.3", {"start": v(-908.05, 2771.77) * mm, "end": v(-1060.45, 2771.77) * mm});
            skLineSegment(sketch, "E6.12.2.3", {"start": v(-1060.45, 2616.2) * mm, "end": v(-450.85, 2616.2) * mm});
            skLineSegment(sketch, "E6.15.2.3", {"start": v(-1063.62, 2616.2) * mm, "end": v(-1063.62, 3225.8) * mm});
            skLineSegment(sketch, "E6.18.2.3", {"start": v(-1060.45, 2768.6) * mm, "end": v(-450.85, 2768.6) * mm});
            skLineSegment(sketch, "E6.21.2.3", {"start": v(-908.05, 3381.37) * mm, "end": v(-1060.45, 3381.37) * mm});
            skLineSegment(sketch, "E6.24.2.3", {"start": v(-1216.02, 2616.2) * mm, "end": v(-1216.02, 3225.8) * mm});
            skLineSegment(sketch, "E6.27.2.3", {"start": v(-1060.45, 2771.77) * mm, "end": v(-1060.45, 3381.37) * mm});
            skLineSegment(sketch, "E6.30.2.3", {"start": v(-606.42, 2460.62) * mm, "end": v(-606.42, 2613.02) * mm});
            skLineSegment(sketch, "E6.33.2.3", {"start": v(-908.05, 2771.77) * mm, "end": v(-908.05, 3381.37) * mm});
            skLineSegment(sketch, "E6.36.2.3", {"start": v(-1216.02, 2460.62) * mm, "end": v(-1216.02, 2613.02) * mm});
            skLineSegment(sketch, "E6.39.2.3", {"start": v(-1063.62, 3225.8) * mm, "end": v(-1216.02, 3225.8) * mm});
            skLineSegment(sketch, "E6.42.2.3", {"start": v(-450.85, 2616.2) * mm, "end": v(-450.85, 2768.6) * mm});
            skLineSegment(sketch, "E6.45.2.3", {"start": v(-1216.02, 2613.02) * mm, "end": v(-606.42, 2613.02) * mm});
            skLineSegment(sketch, "E6.0.2.4", {"start": v(-1828.8, 3073.4) * mm, "end": v(-1219.2, 3073.4) * mm});
            skLineSegment(sketch, "E6.3.2.4", {"start": v(-1676.4, 3228.97) * mm, "end": v(-1828.8, 3228.97) * mm});
            skLineSegment(sketch, "E6.6.2.4", {"start": v(-1673.22, 3228.97) * mm, "end": v(-1673.22, 3381.37) * mm});
            skLineSegment(sketch, "E6.9.2.4", {"start": v(-1520.82, 3384.55) * mm, "end": v(-1673.22, 3384.55) * mm});
            skLineSegment(sketch, "E6.12.2.4", {"start": v(-1673.22, 3228.97) * mm, "end": v(-1063.62, 3228.97) * mm});
            skLineSegment(sketch, "E6.15.2.4", {"start": v(-1676.4, 3228.97) * mm, "end": v(-1676.4, 3838.57) * mm});
            skLineSegment(sketch, "E6.18.2.4", {"start": v(-1673.22, 3381.37) * mm, "end": v(-1063.62, 3381.37) * mm});
            skLineSegment(sketch, "E6.21.2.4", {"start": v(-1520.82, 3994.15) * mm, "end": v(-1673.22, 3994.15) * mm});
            skLineSegment(sketch, "E6.24.2.4", {"start": v(-1828.8, 3228.97) * mm, "end": v(-1828.8, 3838.57) * mm});
            skLineSegment(sketch, "E6.27.2.4", {"start": v(-1673.22, 3384.55) * mm, "end": v(-1673.22, 3994.15) * mm});
            skLineSegment(sketch, "E6.30.2.4", {"start": v(-1219.2, 3073.4) * mm, "end": v(-1219.2, 3225.8) * mm});
            skLineSegment(sketch, "E6.33.2.4", {"start": v(-1520.82, 3384.55) * mm, "end": v(-1520.82, 3994.15) * mm});
            skLineSegment(sketch, "E6.36.2.4", {"start": v(-1828.8, 3073.4) * mm, "end": v(-1828.8, 3225.8) * mm});
            skLineSegment(sketch, "E6.39.2.4", {"start": v(-1676.4, 3838.57) * mm, "end": v(-1828.8, 3838.57) * mm});
            skLineSegment(sketch, "E6.42.2.4", {"start": v(-1063.62, 3228.97) * mm, "end": v(-1063.62, 3381.37) * mm});
            skLineSegment(sketch, "E6.45.2.4", {"start": v(-1828.8, 3225.8) * mm, "end": v(-1219.2, 3225.8) * mm});
            skLineSegment(sketch, "E6.0.3.2", {"start": v(-292.1, 2159) * mm, "end": v(317.5, 2159) * mm});
            skLineSegment(sketch, "E6.3.3.2", {"start": v(-139.7, 2314.57) * mm, "end": v(-292.1, 2314.57) * mm});
            skLineSegment(sketch, "E6.6.3.2", {"start": v(-136.52, 2314.57) * mm, "end": v(-136.52, 2466.97) * mm});
            skLineSegment(sketch, "E6.9.3.2", {"start": v(15.88, 2470.15) * mm, "end": v(-136.52, 2470.15) * mm});
            skLineSegment(sketch, "E6.12.3.2", {"start": v(-136.52, 2314.57) * mm, "end": v(473.08, 2314.57) * mm});
            skLineSegment(sketch, "E6.15.3.2", {"start": v(-139.7, 2314.57) * mm, "end": v(-139.7, 2924.17) * mm});
            skLineSegment(sketch, "E6.18.3.2", {"start": v(-136.52, 2466.97) * mm, "end": v(473.08, 2466.97) * mm});
            skLineSegment(sketch, "E6.21.3.2", {"start": v(15.88, 3079.75) * mm, "end": v(-136.52, 3079.75) * mm});
            skLineSegment(sketch, "E6.24.3.2", {"start": v(-292.1, 2314.57) * mm, "end": v(-292.1, 2924.17) * mm});
            skLineSegment(sketch, "E6.27.3.2", {"start": v(-136.52, 2470.15) * mm, "end": v(-136.52, 3079.75) * mm});
            skLineSegment(sketch, "E6.30.3.2", {"start": v(317.5, 2159) * mm, "end": v(317.5, 2311.4) * mm});
            skLineSegment(sketch, "E6.33.3.2", {"start": v(15.88, 2470.15) * mm, "end": v(15.88, 3079.75) * mm});
            skLineSegment(sketch, "E6.36.3.2", {"start": v(-292.1, 2159) * mm, "end": v(-292.1, 2311.4) * mm});
            skLineSegment(sketch, "E6.39.3.2", {"start": v(-139.7, 2924.17) * mm, "end": v(-292.1, 2924.17) * mm});
            skLineSegment(sketch, "E6.42.3.2", {"start": v(473.08, 2314.57) * mm, "end": v(473.08, 2466.97) * mm});
            skLineSegment(sketch, "E6.45.3.2", {"start": v(-292.1, 2311.4) * mm, "end": v(317.5, 2311.4) * mm});
            skLineSegment(sketch, "E6.0.3.3", {"start": v(-904.87, 2771.77) * mm, "end": v(-295.27, 2771.77) * mm});
            skLineSegment(sketch, "E6.3.3.3", {"start": v(-752.47, 2927.35) * mm, "end": v(-904.87, 2927.35) * mm});
            skLineSegment(sketch, "E6.6.3.3", {"start": v(-749.3, 2927.35) * mm, "end": v(-749.3, 3079.75) * mm});
            skLineSegment(sketch, "E6.9.3.3", {"start": v(-596.9, 3082.92) * mm, "end": v(-749.3, 3082.92) * mm});
            skLineSegment(sketch, "E6.12.3.3", {"start": v(-749.3, 2927.35) * mm, "end": v(-139.7, 2927.35) * mm});
            skLineSegment(sketch, "E6.15.3.3", {"start": v(-752.47, 2927.35) * mm, "end": v(-752.47, 3536.95) * mm});
            skLineSegment(sketch, "E6.18.3.3", {"start": v(-749.3, 3079.75) * mm, "end": v(-139.7, 3079.75) * mm});
            skLineSegment(sketch, "E6.21.3.3", {"start": v(-596.9, 3692.52) * mm, "end": v(-749.3, 3692.52) * mm});
            skLineSegment(sketch, "E6.24.3.3", {"start": v(-904.87, 2927.35) * mm, "end": v(-904.87, 3536.95) * mm});
            skLineSegment(sketch, "E6.27.3.3", {"start": v(-749.3, 3082.92) * mm, "end": v(-749.3, 3692.52) * mm});
            skLineSegment(sketch, "E6.30.3.3", {"start": v(-295.27, 2771.77) * mm, "end": v(-295.27, 2924.17) * mm});
            skLineSegment(sketch, "E6.33.3.3", {"start": v(-596.9, 3082.92) * mm, "end": v(-596.9, 3692.52) * mm});
            skLineSegment(sketch, "E6.36.3.3", {"start": v(-904.87, 2771.77) * mm, "end": v(-904.87, 2924.17) * mm});
            skLineSegment(sketch, "E6.39.3.3", {"start": v(-752.47, 3536.95) * mm, "end": v(-904.87, 3536.95) * mm});
            skLineSegment(sketch, "E6.42.3.3", {"start": v(-139.7, 2927.35) * mm, "end": v(-139.7, 3079.75) * mm});
            skLineSegment(sketch, "E6.45.3.3", {"start": v(-904.87, 2924.17) * mm, "end": v(-295.27, 2924.17) * mm});
            skLineSegment(sketch, "E6.0.3.4", {"start": v(-1517.65, 3384.55) * mm, "end": v(-908.05, 3384.55) * mm});
            skLineSegment(sketch, "E6.3.3.4", {"start": v(-1365.25, 3540.12) * mm, "end": v(-1517.65, 3540.12) * mm});
            skLineSegment(sketch, "E6.6.3.4", {"start": v(-1362.07, 3540.12) * mm, "end": v(-1362.07, 3692.52) * mm});
            skLineSegment(sketch, "E6.9.3.4", {"start": v(-1209.67, 3695.7) * mm, "end": v(-1362.07, 3695.7) * mm});
            skLineSegment(sketch, "E6.12.3.4", {"start": v(-1362.07, 3540.12) * mm, "end": v(-752.47, 3540.12) * mm});
            skLineSegment(sketch, "E6.15.3.4", {"start": v(-1365.25, 3540.12) * mm, "end": v(-1365.25, 4149.72) * mm});
            skLineSegment(sketch, "E6.18.3.4", {"start": v(-1362.07, 3692.52) * mm, "end": v(-752.47, 3692.52) * mm});
            skLineSegment(sketch, "E6.21.3.4", {"start": v(-1209.67, 4305.3) * mm, "end": v(-1362.07, 4305.3) * mm});
            skLineSegment(sketch, "E6.24.3.4", {"start": v(-1517.65, 3540.12) * mm, "end": v(-1517.65, 4149.72) * mm});
            skLineSegment(sketch, "E6.27.3.4", {"start": v(-1362.07, 3695.7) * mm, "end": v(-1362.07, 4305.3) * mm});
            skLineSegment(sketch, "E6.30.3.4", {"start": v(-908.05, 3384.55) * mm, "end": v(-908.05, 3536.95) * mm});
            skLineSegment(sketch, "E6.33.3.4", {"start": v(-1209.67, 3695.7) * mm, "end": v(-1209.67, 4305.3) * mm});
            skLineSegment(sketch, "E6.36.3.4", {"start": v(-1517.65, 3384.55) * mm, "end": v(-1517.65, 3536.95) * mm});
            skLineSegment(sketch, "E6.39.3.4", {"start": v(-1365.25, 4149.72) * mm, "end": v(-1517.65, 4149.72) * mm});
            skLineSegment(sketch, "E6.42.3.4", {"start": v(-752.47, 3540.12) * mm, "end": v(-752.47, 3692.52) * mm});
            skLineSegment(sketch, "E6.45.3.4", {"start": v(-1517.65, 3536.95) * mm, "end": v(-908.05, 3536.95) * mm});
            skLineSegment(sketch, "E6.0.4.2", {"start": v(19.05, 2470.15) * mm, "end": v(628.65, 2470.15) * mm});
            skLineSegment(sketch, "E6.3.4.2", {"start": v(171.45, 2625.72) * mm, "end": v(19.05, 2625.72) * mm});
            skLineSegment(sketch, "E6.6.4.2", {"start": v(174.63, 2625.72) * mm, "end": v(174.63, 2778.12) * mm});
            skLineSegment(sketch, "E6.9.4.2", {"start": v(327.03, 2781.3) * mm, "end": v(174.63, 2781.3) * mm});
            skLineSegment(sketch, "E6.12.4.2", {"start": v(174.63, 2625.72) * mm, "end": v(784.23, 2625.72) * mm});
            skLineSegment(sketch, "E6.15.4.2", {"start": v(171.45, 2625.72) * mm, "end": v(171.45, 3235.32) * mm});
            skLineSegment(sketch, "E6.18.4.2", {"start": v(174.63, 2778.12) * mm, "end": v(784.23, 2778.12) * mm});
            skLineSegment(sketch, "E6.21.4.2", {"start": v(327.03, 3390.9) * mm, "end": v(174.63, 3390.9) * mm});
            skLineSegment(sketch, "E6.24.4.2", {"start": v(19.05, 2625.72) * mm, "end": v(19.05, 3235.32) * mm});
            skLineSegment(sketch, "E6.27.4.2", {"start": v(174.63, 2781.3) * mm, "end": v(174.63, 3390.9) * mm});
            skLineSegment(sketch, "E6.30.4.2", {"start": v(628.65, 2470.15) * mm, "end": v(628.65, 2622.55) * mm});
            skLineSegment(sketch, "E6.33.4.2", {"start": v(327.03, 2781.3) * mm, "end": v(327.03, 3390.9) * mm});
            skLineSegment(sketch, "E6.36.4.2", {"start": v(19.05, 2470.15) * mm, "end": v(19.05, 2622.55) * mm});
            skLineSegment(sketch, "E6.39.4.2", {"start": v(171.45, 3235.32) * mm, "end": v(19.05, 3235.32) * mm});
            skLineSegment(sketch, "E6.42.4.2", {"start": v(784.23, 2625.72) * mm, "end": v(784.23, 2778.12) * mm});
            skLineSegment(sketch, "E6.45.4.2", {"start": v(19.05, 2622.55) * mm, "end": v(628.65, 2622.55) * mm});
            skLineSegment(sketch, "E6.0.4.3", {"start": v(-593.72, 3082.92) * mm, "end": v(15.88, 3082.92) * mm});
            skLineSegment(sketch, "E6.3.4.3", {"start": v(-441.32, 3238.5) * mm, "end": v(-593.72, 3238.5) * mm});
            skLineSegment(sketch, "E6.6.4.3", {"start": v(-438.15, 3238.5) * mm, "end": v(-438.15, 3390.9) * mm});
            skLineSegment(sketch, "E6.9.4.3", {"start": v(-285.75, 3394.07) * mm, "end": v(-438.15, 3394.07) * mm});
            skLineSegment(sketch, "E6.12.4.3", {"start": v(-438.15, 3238.5) * mm, "end": v(171.45, 3238.5) * mm});
            skLineSegment(sketch, "E6.15.4.3", {"start": v(-441.32, 3238.5) * mm, "end": v(-441.32, 3848.1) * mm});
            skLineSegment(sketch, "E6.18.4.3", {"start": v(-438.15, 3390.9) * mm, "end": v(171.45, 3390.9) * mm});
            skLineSegment(sketch, "E6.21.4.3", {"start": v(-285.75, 4003.67) * mm, "end": v(-438.15, 4003.67) * mm});
            skLineSegment(sketch, "E6.24.4.3", {"start": v(-593.72, 3238.5) * mm, "end": v(-593.72, 3848.1) * mm});
            skLineSegment(sketch, "E6.27.4.3", {"start": v(-438.15, 3394.07) * mm, "end": v(-438.15, 4003.67) * mm});
            skLineSegment(sketch, "E6.30.4.3", {"start": v(15.88, 3082.92) * mm, "end": v(15.88, 3235.32) * mm});
            skLineSegment(sketch, "E6.33.4.3", {"start": v(-285.75, 3394.07) * mm, "end": v(-285.75, 4003.67) * mm});
            skLineSegment(sketch, "E6.36.4.3", {"start": v(-593.72, 3082.92) * mm, "end": v(-593.72, 3235.32) * mm});
            skLineSegment(sketch, "E6.39.4.3", {"start": v(-441.32, 3848.1) * mm, "end": v(-593.72, 3848.1) * mm});
            skLineSegment(sketch, "E6.42.4.3", {"start": v(171.45, 3238.5) * mm, "end": v(171.45, 3390.9) * mm});
            skLineSegment(sketch, "E6.45.4.3", {"start": v(-593.72, 3235.32) * mm, "end": v(15.88, 3235.32) * mm});
            skLineSegment(sketch, "E6.0.4.4", {"start": v(-1206.5, 3695.7) * mm, "end": v(-596.9, 3695.7) * mm});
            skLineSegment(sketch, "E6.3.4.4", {"start": v(-1054.1, 3851.27) * mm, "end": v(-1206.5, 3851.27) * mm});
            skLineSegment(sketch, "E6.6.4.4", {"start": v(-1050.92, 3851.27) * mm, "end": v(-1050.92, 4003.67) * mm});
            skLineSegment(sketch, "E6.9.4.4", {"start": v(-898.52, 4006.85) * mm, "end": v(-1050.92, 4006.85) * mm});
            skLineSegment(sketch, "E6.12.4.4", {"start": v(-1050.92, 3851.27) * mm, "end": v(-441.32, 3851.27) * mm});
            skLineSegment(sketch, "E6.15.4.4", {"start": v(-1054.1, 3851.27) * mm, "end": v(-1054.1, 4460.87) * mm});
            skLineSegment(sketch, "E6.18.4.4", {"start": v(-1050.92, 4003.67) * mm, "end": v(-441.32, 4003.67) * mm});
            skLineSegment(sketch, "E6.21.4.4", {"start": v(-898.52, 4616.45) * mm, "end": v(-1050.92, 4616.45) * mm});
            skLineSegment(sketch, "E6.24.4.4", {"start": v(-1206.5, 3851.27) * mm, "end": v(-1206.5, 4460.87) * mm});
            skLineSegment(sketch, "E6.27.4.4", {"start": v(-1050.92, 4006.85) * mm, "end": v(-1050.92, 4616.45) * mm});
            skLineSegment(sketch, "E6.30.4.4", {"start": v(-596.9, 3695.7) * mm, "end": v(-596.9, 3848.1) * mm});
            skLineSegment(sketch, "E6.33.4.4", {"start": v(-898.52, 4006.85) * mm, "end": v(-898.52, 4616.45) * mm});
            skLineSegment(sketch, "E6.36.4.4", {"start": v(-1206.5, 3695.7) * mm, "end": v(-1206.5, 3848.1) * mm});
            skLineSegment(sketch, "E6.39.4.4", {"start": v(-1054.1, 4460.87) * mm, "end": v(-1206.5, 4460.87) * mm});
            skLineSegment(sketch, "E6.42.4.4", {"start": v(-441.32, 3851.27) * mm, "end": v(-441.32, 4003.67) * mm});
            skLineSegment(sketch, "E6.45.4.4", {"start": v(-1206.5, 3848.1) * mm, "end": v(-596.9, 3848.1) * mm});
            skLineSegment(sketch, "E6.0.5.2", {"start": v(330.2, 2781.3) * mm, "end": v(939.8, 2781.3) * mm});
            skLineSegment(sketch, "E6.3.5.2", {"start": v(482.6, 2936.87) * mm, "end": v(330.2, 2936.87) * mm});
            skLineSegment(sketch, "E6.6.5.2", {"start": v(485.78, 2936.87) * mm, "end": v(485.78, 3089.27) * mm});
            skLineSegment(sketch, "E6.9.5.2", {"start": v(638.18, 3092.45) * mm, "end": v(485.78, 3092.45) * mm});
            skLineSegment(sketch, "E6.12.5.2", {"start": v(485.78, 2936.87) * mm, "end": v(1095.38, 2936.87) * mm});
            skLineSegment(sketch, "E6.15.5.2", {"start": v(482.6, 2936.87) * mm, "end": v(482.6, 3546.47) * mm});
            skLineSegment(sketch, "E6.18.5.2", {"start": v(485.78, 3089.27) * mm, "end": v(1095.38, 3089.27) * mm});
            skLineSegment(sketch, "E6.21.5.2", {"start": v(638.18, 3702.05) * mm, "end": v(485.78, 3702.05) * mm});
            skLineSegment(sketch, "E6.24.5.2", {"start": v(330.2, 2936.87) * mm, "end": v(330.2, 3546.47) * mm});
            skLineSegment(sketch, "E6.27.5.2", {"start": v(485.78, 3092.45) * mm, "end": v(485.78, 3702.05) * mm});
            skLineSegment(sketch, "E6.30.5.2", {"start": v(939.8, 2781.3) * mm, "end": v(939.8, 2933.7) * mm});
            skLineSegment(sketch, "E6.33.5.2", {"start": v(638.18, 3092.45) * mm, "end": v(638.18, 3702.05) * mm});
            skLineSegment(sketch, "E6.36.5.2", {"start": v(330.2, 2781.3) * mm, "end": v(330.2, 2933.7) * mm});
            skLineSegment(sketch, "E6.39.5.2", {"start": v(482.6, 3546.47) * mm, "end": v(330.2, 3546.47) * mm});
            skLineSegment(sketch, "E6.42.5.2", {"start": v(1095.38, 2936.87) * mm, "end": v(1095.38, 3089.27) * mm});
            skLineSegment(sketch, "E6.45.5.2", {"start": v(330.2, 2933.7) * mm, "end": v(939.8, 2933.7) * mm});
            skLineSegment(sketch, "E6.0.5.3", {"start": v(-282.57, 3394.07) * mm, "end": v(327.03, 3394.07) * mm});
            skLineSegment(sketch, "E6.3.5.3", {"start": v(-130.17, 3549.65) * mm, "end": v(-282.57, 3549.65) * mm});
            skLineSegment(sketch, "E6.6.5.3", {"start": v(-127, 3549.65) * mm, "end": v(-127, 3702.05) * mm});
            skLineSegment(sketch, "E6.9.5.3", {"start": v(25.4, 3705.22) * mm, "end": v(-127, 3705.22) * mm});
            skLineSegment(sketch, "E6.12.5.3", {"start": v(-127, 3549.65) * mm, "end": v(482.6, 3549.65) * mm});
            skLineSegment(sketch, "E6.15.5.3", {"start": v(-130.17, 3549.65) * mm, "end": v(-130.17, 4159.25) * mm});
            skLineSegment(sketch, "E6.18.5.3", {"start": v(-127, 3702.05) * mm, "end": v(482.6, 3702.05) * mm});
            skLineSegment(sketch, "E6.21.5.3", {"start": v(25.4, 4314.82) * mm, "end": v(-127, 4314.82) * mm});
            skLineSegment(sketch, "E6.24.5.3", {"start": v(-282.57, 3549.65) * mm, "end": v(-282.57, 4159.25) * mm});
            skLineSegment(sketch, "E6.27.5.3", {"start": v(-127, 3705.22) * mm, "end": v(-127, 4314.82) * mm});
            skLineSegment(sketch, "E6.30.5.3", {"start": v(327.03, 3394.07) * mm, "end": v(327.03, 3546.47) * mm});
            skLineSegment(sketch, "E6.33.5.3", {"start": v(25.4, 3705.22) * mm, "end": v(25.4, 4314.82) * mm});
            skLineSegment(sketch, "E6.36.5.3", {"start": v(-282.57, 3394.07) * mm, "end": v(-282.57, 3546.47) * mm});
            skLineSegment(sketch, "E6.39.5.3", {"start": v(-130.17, 4159.25) * mm, "end": v(-282.57, 4159.25) * mm});
            skLineSegment(sketch, "E6.42.5.3", {"start": v(482.6, 3549.65) * mm, "end": v(482.6, 3702.05) * mm});
            skLineSegment(sketch, "E6.45.5.3", {"start": v(-282.57, 3546.47) * mm, "end": v(327.03, 3546.47) * mm});
            skLineSegment(sketch, "E6.0.5.4", {"start": v(-895.35, 4006.85) * mm, "end": v(-285.75, 4006.85) * mm});
            skLineSegment(sketch, "E6.3.5.4", {"start": v(-742.95, 4162.42) * mm, "end": v(-895.35, 4162.42) * mm});
            skLineSegment(sketch, "E6.6.5.4", {"start": v(-739.77, 4162.42) * mm, "end": v(-739.77, 4314.82) * mm});
            skLineSegment(sketch, "E6.9.5.4", {"start": v(-587.37, 4318) * mm, "end": v(-739.77, 4318) * mm});
            skLineSegment(sketch, "E6.12.5.4", {"start": v(-739.77, 4162.42) * mm, "end": v(-130.17, 4162.42) * mm});
            skLineSegment(sketch, "E6.15.5.4", {"start": v(-742.95, 4162.42) * mm, "end": v(-742.95, 4772.02) * mm});
            skLineSegment(sketch, "E6.18.5.4", {"start": v(-739.77, 4314.82) * mm, "end": v(-130.17, 4314.82) * mm});
            skLineSegment(sketch, "E6.21.5.4", {"start": v(-587.37, 4927.6) * mm, "end": v(-739.77, 4927.6) * mm});
            skLineSegment(sketch, "E6.24.5.4", {"start": v(-895.35, 4162.42) * mm, "end": v(-895.35, 4772.02) * mm});
            skLineSegment(sketch, "E6.27.5.4", {"start": v(-739.77, 4318) * mm, "end": v(-739.77, 4927.6) * mm});
            skLineSegment(sketch, "E6.30.5.4", {"start": v(-285.75, 4006.85) * mm, "end": v(-285.75, 4159.25) * mm});
            skLineSegment(sketch, "E6.33.5.4", {"start": v(-587.37, 4318) * mm, "end": v(-587.37, 4927.6) * mm});
            skLineSegment(sketch, "E6.36.5.4", {"start": v(-895.35, 4006.85) * mm, "end": v(-895.35, 4159.25) * mm});
            skLineSegment(sketch, "E6.39.5.4", {"start": v(-742.95, 4772.02) * mm, "end": v(-895.35, 4772.02) * mm});
            skLineSegment(sketch, "E6.42.5.4", {"start": v(-130.17, 4162.42) * mm, "end": v(-130.17, 4314.82) * mm});
            skLineSegment(sketch, "E6.45.5.4", {"start": v(-895.35, 4159.25) * mm, "end": v(-285.75, 4159.25) * mm});
            skLineSegment(sketch, "E7.0.6.0", {"start": v(1866.9, 1866.9) * mm, "end": v(2476.5, 1866.9) * mm});
            skLineSegment(sketch, "E7.3.6.0", {"start": v(2019.3, 2022.47) * mm, "end": v(1866.9, 2022.47) * mm});
            skLineSegment(sketch, "E7.6.6.0", {"start": v(2022.48, 2022.47) * mm, "end": v(2022.48, 2174.87) * mm});
            skLineSegment(sketch, "E7.9.6.0", {"start": v(2174.88, 2178.05) * mm, "end": v(2022.48, 2178.05) * mm});
            skLineSegment(sketch, "E7.12.6.0", {"start": v(2022.48, 2022.47) * mm, "end": v(2632.08, 2022.47) * mm});
            skLineSegment(sketch, "E7.15.6.0", {"start": v(2019.3, 2022.47) * mm, "end": v(2019.3, 2632.07) * mm});
            skLineSegment(sketch, "E7.18.6.0", {"start": v(2022.48, 2174.87) * mm, "end": v(2632.08, 2174.87) * mm});
            skLineSegment(sketch, "E7.21.6.0", {"start": v(2174.88, 2787.65) * mm, "end": v(2022.48, 2787.65) * mm});
            skLineSegment(sketch, "E7.24.6.0", {"start": v(1866.9, 2022.47) * mm, "end": v(1866.9, 2632.07) * mm});
            skLineSegment(sketch, "E7.27.6.0", {"start": v(2022.48, 2178.05) * mm, "end": v(2022.48, 2787.65) * mm});
            skLineSegment(sketch, "E7.30.6.0", {"start": v(2476.5, 1866.9) * mm, "end": v(2476.5, 2019.3) * mm});
            skLineSegment(sketch, "E7.33.6.0", {"start": v(2174.88, 2178.05) * mm, "end": v(2174.88, 2787.65) * mm});
            skLineSegment(sketch, "E7.36.6.0", {"start": v(1866.9, 1866.9) * mm, "end": v(1866.9, 2019.3) * mm});
            skLineSegment(sketch, "E7.39.6.0", {"start": v(2019.3, 2632.07) * mm, "end": v(1866.9, 2632.07) * mm});
            skLineSegment(sketch, "E7.42.6.0", {"start": v(2632.08, 2022.47) * mm, "end": v(2632.08, 2174.87) * mm});
            skLineSegment(sketch, "E7.45.6.0", {"start": v(1866.9, 2019.3) * mm, "end": v(2476.5, 2019.3) * mm});
            skLineSegment(sketch, "E7.0.6.1", {"start": v(1254.13, 2479.67) * mm, "end": v(1863.73, 2479.67) * mm});
            skLineSegment(sketch, "E7.3.6.1", {"start": v(1406.53, 2635.25) * mm, "end": v(1254.13, 2635.25) * mm});
            skLineSegment(sketch, "E7.6.6.1", {"start": v(1409.7, 2635.25) * mm, "end": v(1409.7, 2787.65) * mm});
            skLineSegment(sketch, "E7.9.6.1", {"start": v(1562.1, 2790.82) * mm, "end": v(1409.7, 2790.82) * mm});
            skLineSegment(sketch, "E7.12.6.1", {"start": v(1409.7, 2635.25) * mm, "end": v(2019.3, 2635.25) * mm});
            skLineSegment(sketch, "E7.15.6.1", {"start": v(1406.53, 2635.25) * mm, "end": v(1406.53, 3244.85) * mm});
            skLineSegment(sketch, "E7.18.6.1", {"start": v(1409.7, 2787.65) * mm, "end": v(2019.3, 2787.65) * mm});
            skLineSegment(sketch, "E7.21.6.1", {"start": v(1562.1, 3400.42) * mm, "end": v(1409.7, 3400.42) * mm});
            skLineSegment(sketch, "E7.24.6.1", {"start": v(1254.13, 2635.25) * mm, "end": v(1254.13, 3244.85) * mm});
            skLineSegment(sketch, "E7.27.6.1", {"start": v(1409.7, 2790.82) * mm, "end": v(1409.7, 3400.42) * mm});
            skLineSegment(sketch, "E7.30.6.1", {"start": v(1863.73, 2479.67) * mm, "end": v(1863.73, 2632.07) * mm});
            skLineSegment(sketch, "E7.33.6.1", {"start": v(1562.1, 2790.82) * mm, "end": v(1562.1, 3400.42) * mm});
            skLineSegment(sketch, "E7.36.6.1", {"start": v(1254.13, 2479.67) * mm, "end": v(1254.13, 2632.07) * mm});
            skLineSegment(sketch, "E7.39.6.1", {"start": v(1406.53, 3244.85) * mm, "end": v(1254.13, 3244.85) * mm});
            skLineSegment(sketch, "E7.42.6.1", {"start": v(2019.3, 2635.25) * mm, "end": v(2019.3, 2787.65) * mm});
            skLineSegment(sketch, "E7.45.6.1", {"start": v(1254.13, 2632.07) * mm, "end": v(1863.73, 2632.07) * mm});
            skLineSegment(sketch, "E7.0.6.2", {"start": v(641.35, 3092.45) * mm, "end": v(1250.95, 3092.45) * mm});
            skLineSegment(sketch, "E7.3.6.2", {"start": v(793.75, 3248.02) * mm, "end": v(641.35, 3248.02) * mm});
            skLineSegment(sketch, "E7.6.6.2", {"start": v(796.92, 3248.02) * mm, "end": v(796.92, 3400.42) * mm});
            skLineSegment(sketch, "E7.9.6.2", {"start": v(949.32, 3403.6) * mm, "end": v(796.92, 3403.6) * mm});
            skLineSegment(sketch, "E7.12.6.2", {"start": v(796.92, 3248.02) * mm, "end": v(1406.52, 3248.02) * mm});
            skLineSegment(sketch, "E7.15.6.2", {"start": v(793.75, 3248.02) * mm, "end": v(793.75, 3857.62) * mm});
            skLineSegment(sketch, "E7.18.6.2", {"start": v(796.92, 3400.42) * mm, "end": v(1406.52, 3400.42) * mm});
            skLineSegment(sketch, "E7.21.6.2", {"start": v(949.32, 4013.2) * mm, "end": v(796.92, 4013.2) * mm});
            skLineSegment(sketch, "E7.24.6.2", {"start": v(641.35, 3248.02) * mm, "end": v(641.35, 3857.62) * mm});
            skLineSegment(sketch, "E7.27.6.2", {"start": v(796.92, 3403.6) * mm, "end": v(796.92, 4013.2) * mm});
            skLineSegment(sketch, "E7.30.6.2", {"start": v(1250.95, 3092.45) * mm, "end": v(1250.95, 3244.85) * mm});
            skLineSegment(sketch, "E7.33.6.2", {"start": v(949.32, 3403.6) * mm, "end": v(949.32, 4013.2) * mm});
            skLineSegment(sketch, "E7.36.6.2", {"start": v(641.35, 3092.45) * mm, "end": v(641.35, 3244.85) * mm});
            skLineSegment(sketch, "E7.39.6.2", {"start": v(793.75, 3857.62) * mm, "end": v(641.35, 3857.62) * mm});
            skLineSegment(sketch, "E7.42.6.2", {"start": v(1406.52, 3248.02) * mm, "end": v(1406.52, 3400.42) * mm});
            skLineSegment(sketch, "E7.45.6.2", {"start": v(641.35, 3244.85) * mm, "end": v(1250.95, 3244.85) * mm});
            skLineSegment(sketch, "E7.0.6.3", {"start": v(28.57, 3705.22) * mm, "end": v(638.17, 3705.22) * mm});
            skLineSegment(sketch, "E7.3.6.3", {"start": v(180.97, 3860.8) * mm, "end": v(28.57, 3860.8) * mm});
            skLineSegment(sketch, "E7.6.6.3", {"start": v(184.15, 3860.8) * mm, "end": v(184.15, 4013.2) * mm});
            skLineSegment(sketch, "E7.9.6.3", {"start": v(336.55, 4016.37) * mm, "end": v(184.15, 4016.37) * mm});
            skLineSegment(sketch, "E7.12.6.3", {"start": v(184.15, 3860.8) * mm, "end": v(793.75, 3860.8) * mm});
            skLineSegment(sketch, "E7.15.6.3", {"start": v(180.97, 3860.8) * mm, "end": v(180.97, 4470.4) * mm});
            skLineSegment(sketch, "E7.18.6.3", {"start": v(184.15, 4013.2) * mm, "end": v(793.75, 4013.2) * mm});
            skLineSegment(sketch, "E7.21.6.3", {"start": v(336.55, 4625.97) * mm, "end": v(184.15, 4625.97) * mm});
            skLineSegment(sketch, "E7.24.6.3", {"start": v(28.57, 3860.8) * mm, "end": v(28.57, 4470.4) * mm});
            skLineSegment(sketch, "E7.27.6.3", {"start": v(184.15, 4016.37) * mm, "end": v(184.15, 4625.97) * mm});
            skLineSegment(sketch, "E7.30.6.3", {"start": v(638.17, 3705.22) * mm, "end": v(638.17, 3857.62) * mm});
            skLineSegment(sketch, "E7.33.6.3", {"start": v(336.55, 4016.37) * mm, "end": v(336.55, 4625.97) * mm});
            skLineSegment(sketch, "E7.36.6.3", {"start": v(28.57, 3705.22) * mm, "end": v(28.57, 3857.62) * mm});
            skLineSegment(sketch, "E7.39.6.3", {"start": v(180.97, 4470.4) * mm, "end": v(28.57, 4470.4) * mm});
            skLineSegment(sketch, "E7.42.6.3", {"start": v(793.75, 3860.8) * mm, "end": v(793.75, 4013.2) * mm});
            skLineSegment(sketch, "E7.45.6.3", {"start": v(28.57, 3857.62) * mm, "end": v(638.17, 3857.62) * mm});
            skLineSegment(sketch, "E7.0.6.4", {"start": v(-584.2, 4318) * mm, "end": v(25.4, 4318) * mm});
            skLineSegment(sketch, "E7.3.6.4", {"start": v(-431.8, 4473.57) * mm, "end": v(-584.2, 4473.57) * mm});
            skLineSegment(sketch, "E7.6.6.4", {"start": v(-428.63, 4473.57) * mm, "end": v(-428.63, 4625.97) * mm});
            skLineSegment(sketch, "E7.9.6.4", {"start": v(-276.23, 4629.15) * mm, "end": v(-428.63, 4629.15) * mm});
            skLineSegment(sketch, "E7.12.6.4", {"start": v(-428.63, 4473.57) * mm, "end": v(180.97, 4473.57) * mm});
            skLineSegment(sketch, "E7.15.6.4", {"start": v(-431.8, 4473.57) * mm, "end": v(-431.8, 5083.18) * mm});
            skLineSegment(sketch, "E7.18.6.4", {"start": v(-428.63, 4625.97) * mm, "end": v(180.97, 4625.97) * mm});
            skLineSegment(sketch, "E7.21.6.4", {"start": v(-276.23, 5238.75) * mm, "end": v(-428.63, 5238.75) * mm});
            skLineSegment(sketch, "E7.24.6.4", {"start": v(-584.2, 4473.57) * mm, "end": v(-584.2, 5083.18) * mm});
            skLineSegment(sketch, "E7.27.6.4", {"start": v(-428.63, 4629.15) * mm, "end": v(-428.63, 5238.75) * mm});
            skLineSegment(sketch, "E7.30.6.4", {"start": v(25.4, 4318) * mm, "end": v(25.4, 4470.4) * mm});
            skLineSegment(sketch, "E7.33.6.4", {"start": v(-276.23, 4629.15) * mm, "end": v(-276.23, 5238.75) * mm});
            skLineSegment(sketch, "E7.36.6.4", {"start": v(-584.2, 4318) * mm, "end": v(-584.2, 4470.4) * mm});
            skLineSegment(sketch, "E7.39.6.4", {"start": v(-431.8, 5083.18) * mm, "end": v(-584.2, 5083.18) * mm});
            skLineSegment(sketch, "E7.42.6.4", {"start": v(180.97, 4473.57) * mm, "end": v(180.97, 4625.97) * mm});
            skLineSegment(sketch, "E7.45.6.4", {"start": v(-584.2, 4470.4) * mm, "end": v(25.4, 4470.4) * mm});
            skLineSegment(sketch, "E7.0.7.0", {"start": v(2178.05, 2178.05) * mm, "end": v(2787.65, 2178.05) * mm});
            skLineSegment(sketch, "E7.3.7.0", {"start": v(2330.45, 2333.62) * mm, "end": v(2178.05, 2333.62) * mm});
            skLineSegment(sketch, "E7.6.7.0", {"start": v(2333.63, 2333.62) * mm, "end": v(2333.63, 2486.02) * mm});
            skLineSegment(sketch, "E7.9.7.0", {"start": v(2486.03, 2489.2) * mm, "end": v(2333.63, 2489.2) * mm});
            skLineSegment(sketch, "E7.12.7.0", {"start": v(2333.63, 2333.62) * mm, "end": v(2943.23, 2333.62) * mm});
            skLineSegment(sketch, "E7.15.7.0", {"start": v(2330.45, 2333.62) * mm, "end": v(2330.45, 2943.22) * mm});
            skLineSegment(sketch, "E7.18.7.0", {"start": v(2333.63, 2486.02) * mm, "end": v(2943.23, 2486.02) * mm});
            skLineSegment(sketch, "E7.21.7.0", {"start": v(2486.03, 3098.8) * mm, "end": v(2333.63, 3098.8) * mm});
            skLineSegment(sketch, "E7.24.7.0", {"start": v(2178.05, 2333.62) * mm, "end": v(2178.05, 2943.22) * mm});
            skLineSegment(sketch, "E7.27.7.0", {"start": v(2333.63, 2489.2) * mm, "end": v(2333.63, 3098.8) * mm});
            skLineSegment(sketch, "E7.30.7.0", {"start": v(2787.65, 2178.05) * mm, "end": v(2787.65, 2330.45) * mm});
            skLineSegment(sketch, "E7.33.7.0", {"start": v(2486.03, 2489.2) * mm, "end": v(2486.03, 3098.8) * mm});
            skLineSegment(sketch, "E7.36.7.0", {"start": v(2178.05, 2178.05) * mm, "end": v(2178.05, 2330.45) * mm});
            skLineSegment(sketch, "E7.39.7.0", {"start": v(2330.45, 2943.22) * mm, "end": v(2178.05, 2943.22) * mm});
            skLineSegment(sketch, "E7.42.7.0", {"start": v(2943.23, 2333.62) * mm, "end": v(2943.23, 2486.02) * mm});
            skLineSegment(sketch, "E7.45.7.0", {"start": v(2178.05, 2330.45) * mm, "end": v(2787.65, 2330.45) * mm});
            skLineSegment(sketch, "E7.0.7.1", {"start": v(1565.28, 2790.82) * mm, "end": v(2174.88, 2790.82) * mm});
            skLineSegment(sketch, "E7.3.7.1", {"start": v(1717.68, 2946.4) * mm, "end": v(1565.28, 2946.4) * mm});
            skLineSegment(sketch, "E7.6.7.1", {"start": v(1720.85, 2946.4) * mm, "end": v(1720.85, 3098.8) * mm});
            skLineSegment(sketch, "E7.9.7.1", {"start": v(1873.25, 3101.97) * mm, "end": v(1720.85, 3101.97) * mm});
            skLineSegment(sketch, "E7.12.7.1", {"start": v(1720.85, 2946.4) * mm, "end": v(2330.45, 2946.4) * mm});
            skLineSegment(sketch, "E7.15.7.1", {"start": v(1717.68, 2946.4) * mm, "end": v(1717.68, 3556) * mm});
            skLineSegment(sketch, "E7.18.7.1", {"start": v(1720.85, 3098.8) * mm, "end": v(2330.45, 3098.8) * mm});
            skLineSegment(sketch, "E7.21.7.1", {"start": v(1873.25, 3711.57) * mm, "end": v(1720.85, 3711.57) * mm});
            skLineSegment(sketch, "E7.24.7.1", {"start": v(1565.28, 2946.4) * mm, "end": v(1565.28, 3556) * mm});
            skLineSegment(sketch, "E7.27.7.1", {"start": v(1720.85, 3101.97) * mm, "end": v(1720.85, 3711.57) * mm});
            skLineSegment(sketch, "E7.30.7.1", {"start": v(2174.88, 2790.82) * mm, "end": v(2174.88, 2943.22) * mm});
            skLineSegment(sketch, "E7.33.7.1", {"start": v(1873.25, 3101.97) * mm, "end": v(1873.25, 3711.57) * mm});
            skLineSegment(sketch, "E7.36.7.1", {"start": v(1565.28, 2790.82) * mm, "end": v(1565.28, 2943.22) * mm});
            skLineSegment(sketch, "E7.39.7.1", {"start": v(1717.68, 3556) * mm, "end": v(1565.28, 3556) * mm});
            skLineSegment(sketch, "E7.42.7.1", {"start": v(2330.45, 2946.4) * mm, "end": v(2330.45, 3098.8) * mm});
            skLineSegment(sketch, "E7.45.7.1", {"start": v(1565.28, 2943.22) * mm, "end": v(2174.88, 2943.22) * mm});
            skLineSegment(sketch, "E7.0.7.2", {"start": v(952.5, 3403.6) * mm, "end": v(1562.1, 3403.6) * mm});
            skLineSegment(sketch, "E7.3.7.2", {"start": v(1104.9, 3559.17) * mm, "end": v(952.5, 3559.17) * mm});
            skLineSegment(sketch, "E7.6.7.2", {"start": v(1108.07, 3559.17) * mm, "end": v(1108.07, 3711.57) * mm});
            skLineSegment(sketch, "E7.9.7.2", {"start": v(1260.47, 3714.75) * mm, "end": v(1108.07, 3714.75) * mm});
            skLineSegment(sketch, "E7.12.7.2", {"start": v(1108.07, 3559.17) * mm, "end": v(1717.67, 3559.17) * mm});
            skLineSegment(sketch, "E7.15.7.2", {"start": v(1104.9, 3559.17) * mm, "end": v(1104.9, 4168.77) * mm});
            skLineSegment(sketch, "E7.18.7.2", {"start": v(1108.07, 3711.57) * mm, "end": v(1717.67, 3711.57) * mm});
            skLineSegment(sketch, "E7.21.7.2", {"start": v(1260.47, 4324.35) * mm, "end": v(1108.07, 4324.35) * mm});
            skLineSegment(sketch, "E7.24.7.2", {"start": v(952.5, 3559.17) * mm, "end": v(952.5, 4168.77) * mm});
            skLineSegment(sketch, "E7.27.7.2", {"start": v(1108.07, 3714.75) * mm, "end": v(1108.07, 4324.35) * mm});
            skLineSegment(sketch, "E7.30.7.2", {"start": v(1562.1, 3403.6) * mm, "end": v(1562.1, 3556) * mm});
            skLineSegment(sketch, "E7.33.7.2", {"start": v(1260.47, 3714.75) * mm, "end": v(1260.47, 4324.35) * mm});
            skLineSegment(sketch, "E7.36.7.2", {"start": v(952.5, 3403.6) * mm, "end": v(952.5, 3556) * mm});
            skLineSegment(sketch, "E7.39.7.2", {"start": v(1104.9, 4168.77) * mm, "end": v(952.5, 4168.77) * mm});
            skLineSegment(sketch, "E7.42.7.2", {"start": v(1717.67, 3559.17) * mm, "end": v(1717.67, 3711.57) * mm});
            skLineSegment(sketch, "E7.45.7.2", {"start": v(952.5, 3556) * mm, "end": v(1562.1, 3556) * mm});
            skLineSegment(sketch, "E7.0.7.3", {"start": v(339.72, 4016.38) * mm, "end": v(949.32, 4016.38) * mm});
            skLineSegment(sketch, "E7.3.7.3", {"start": v(492.12, 4171.95) * mm, "end": v(339.72, 4171.95) * mm});
            skLineSegment(sketch, "E7.6.7.3", {"start": v(495.3, 4171.95) * mm, "end": v(495.3, 4324.35) * mm});
            skLineSegment(sketch, "E7.9.7.3", {"start": v(647.7, 4327.52) * mm, "end": v(495.3, 4327.52) * mm});
            skLineSegment(sketch, "E7.12.7.3", {"start": v(495.3, 4171.95) * mm, "end": v(1104.9, 4171.95) * mm});
            skLineSegment(sketch, "E7.15.7.3", {"start": v(492.12, 4171.95) * mm, "end": v(492.12, 4781.55) * mm});
            skLineSegment(sketch, "E7.18.7.3", {"start": v(495.3, 4324.35) * mm, "end": v(1104.9, 4324.35) * mm});
            skLineSegment(sketch, "E7.21.7.3", {"start": v(647.7, 4937.12) * mm, "end": v(495.3, 4937.12) * mm});
            skLineSegment(sketch, "E7.24.7.3", {"start": v(339.72, 4171.95) * mm, "end": v(339.72, 4781.55) * mm});
            skLineSegment(sketch, "E7.27.7.3", {"start": v(495.3, 4327.52) * mm, "end": v(495.3, 4937.12) * mm});
            skLineSegment(sketch, "E7.30.7.3", {"start": v(949.32, 4016.38) * mm, "end": v(949.32, 4168.78) * mm});
            skLineSegment(sketch, "E7.33.7.3", {"start": v(647.7, 4327.52) * mm, "end": v(647.7, 4937.12) * mm});
            skLineSegment(sketch, "E7.36.7.3", {"start": v(339.72, 4016.38) * mm, "end": v(339.72, 4168.78) * mm});
            skLineSegment(sketch, "E7.39.7.3", {"start": v(492.12, 4781.55) * mm, "end": v(339.72, 4781.55) * mm});
            skLineSegment(sketch, "E7.42.7.3", {"start": v(1104.9, 4171.95) * mm, "end": v(1104.9, 4324.35) * mm});
            skLineSegment(sketch, "E7.45.7.3", {"start": v(339.72, 4168.78) * mm, "end": v(949.32, 4168.78) * mm});
            skLineSegment(sketch, "E7.0.7.4", {"start": v(-273.05, 4629.15) * mm, "end": v(336.55, 4629.15) * mm});
            skLineSegment(sketch, "E7.3.7.4", {"start": v(-120.65, 4784.72) * mm, "end": v(-273.05, 4784.72) * mm});
            skLineSegment(sketch, "E7.6.7.4", {"start": v(-117.48, 4784.72) * mm, "end": v(-117.48, 4937.12) * mm});
            skLineSegment(sketch, "E7.9.7.4", {"start": v(34.92, 4940.3) * mm, "end": v(-117.48, 4940.3) * mm});
            skLineSegment(sketch, "E7.12.7.4", {"start": v(-117.48, 4784.72) * mm, "end": v(492.12, 4784.72) * mm});
            skLineSegment(sketch, "E7.15.7.4", {"start": v(-120.65, 4784.72) * mm, "end": v(-120.65, 5394.32) * mm});
            skLineSegment(sketch, "E7.18.7.4", {"start": v(-117.48, 4937.12) * mm, "end": v(492.12, 4937.12) * mm});
            skLineSegment(sketch, "E7.21.7.4", {"start": v(34.92, 5549.9) * mm, "end": v(-117.48, 5549.9) * mm});
            skLineSegment(sketch, "E7.24.7.4", {"start": v(-273.05, 4784.72) * mm, "end": v(-273.05, 5394.32) * mm});
            skLineSegment(sketch, "E7.27.7.4", {"start": v(-117.48, 4940.3) * mm, "end": v(-117.48, 5549.9) * mm});
            skLineSegment(sketch, "E7.30.7.4", {"start": v(336.55, 4629.15) * mm, "end": v(336.55, 4781.55) * mm});
            skLineSegment(sketch, "E7.33.7.4", {"start": v(34.92, 4940.3) * mm, "end": v(34.92, 5549.9) * mm});
            skLineSegment(sketch, "E7.36.7.4", {"start": v(-273.05, 4629.15) * mm, "end": v(-273.05, 4781.55) * mm});
            skLineSegment(sketch, "E7.39.7.4", {"start": v(-120.65, 5394.32) * mm, "end": v(-273.05, 5394.32) * mm});
            skLineSegment(sketch, "E7.42.7.4", {"start": v(492.12, 4784.72) * mm, "end": v(492.12, 4937.12) * mm});
            skLineSegment(sketch, "E7.45.7.4", {"start": v(-273.05, 4781.55) * mm, "end": v(336.55, 4781.55) * mm});
            skLineSegment(sketch, "E8.0.8.0", {"start": v(2489.2, 2489.2) * mm, "end": v(3098.8, 2489.2) * mm});
            skLineSegment(sketch, "E8.3.8.0", {"start": v(2641.6, 2644.77) * mm, "end": v(2489.2, 2644.77) * mm});
            skLineSegment(sketch, "E8.6.8.0", {"start": v(2644.78, 2644.77) * mm, "end": v(2644.78, 2797.17) * mm});
            skLineSegment(sketch, "E8.9.8.0", {"start": v(2797.18, 2800.35) * mm, "end": v(2644.78, 2800.35) * mm});
            skLineSegment(sketch, "E8.12.8.0", {"start": v(2644.78, 2644.77) * mm, "end": v(3254.38, 2644.77) * mm});
            skLineSegment(sketch, "E8.15.8.0", {"start": v(2641.6, 2644.77) * mm, "end": v(2641.6, 3254.37) * mm});
            skLineSegment(sketch, "E8.18.8.0", {"start": v(2644.78, 2797.17) * mm, "end": v(3254.38, 2797.17) * mm});
            skLineSegment(sketch, "E8.21.8.0", {"start": v(2797.18, 3409.95) * mm, "end": v(2644.78, 3409.95) * mm});
            skLineSegment(sketch, "E8.24.8.0", {"start": v(2489.2, 2644.77) * mm, "end": v(2489.2, 3254.37) * mm});
            skLineSegment(sketch, "E8.27.8.0", {"start": v(2644.78, 2800.35) * mm, "end": v(2644.78, 3409.95) * mm});
            skLineSegment(sketch, "E8.30.8.0", {"start": v(3098.8, 2489.2) * mm, "end": v(3098.8, 2641.6) * mm});
            skLineSegment(sketch, "E8.33.8.0", {"start": v(2797.18, 2800.35) * mm, "end": v(2797.18, 3409.95) * mm});
            skLineSegment(sketch, "E8.36.8.0", {"start": v(2489.2, 2489.2) * mm, "end": v(2489.2, 2641.6) * mm});
            skLineSegment(sketch, "E8.39.8.0", {"start": v(2641.6, 3254.37) * mm, "end": v(2489.2, 3254.37) * mm});
            skLineSegment(sketch, "E8.42.8.0", {"start": v(3254.38, 2644.77) * mm, "end": v(3254.38, 2797.17) * mm});
            skLineSegment(sketch, "E8.45.8.0", {"start": v(2489.2, 2641.6) * mm, "end": v(3098.8, 2641.6) * mm});
            skLineSegment(sketch, "E8.0.8.1", {"start": v(1876.43, 3101.97) * mm, "end": v(2486.03, 3101.97) * mm});
            skLineSegment(sketch, "E8.3.8.1", {"start": v(2028.83, 3257.55) * mm, "end": v(1876.43, 3257.55) * mm});
            skLineSegment(sketch, "E8.6.8.1", {"start": v(2032, 3257.55) * mm, "end": v(2032, 3409.95) * mm});
            skLineSegment(sketch, "E8.9.8.1", {"start": v(2184.4, 3413.12) * mm, "end": v(2032, 3413.12) * mm});
            skLineSegment(sketch, "E8.12.8.1", {"start": v(2032, 3257.55) * mm, "end": v(2641.6, 3257.55) * mm});
            skLineSegment(sketch, "E8.15.8.1", {"start": v(2028.83, 3257.55) * mm, "end": v(2028.83, 3867.15) * mm});
            skLineSegment(sketch, "E8.18.8.1", {"start": v(2032, 3409.95) * mm, "end": v(2641.6, 3409.95) * mm});
            skLineSegment(sketch, "E8.21.8.1", {"start": v(2184.4, 4022.72) * mm, "end": v(2032, 4022.72) * mm});
            skLineSegment(sketch, "E8.24.8.1", {"start": v(1876.43, 3257.55) * mm, "end": v(1876.43, 3867.15) * mm});
            skLineSegment(sketch, "E8.27.8.1", {"start": v(2032, 3413.12) * mm, "end": v(2032, 4022.72) * mm});
            skLineSegment(sketch, "E8.30.8.1", {"start": v(2486.03, 3101.97) * mm, "end": v(2486.03, 3254.37) * mm});
            skLineSegment(sketch, "E8.33.8.1", {"start": v(2184.4, 3413.12) * mm, "end": v(2184.4, 4022.72) * mm});
            skLineSegment(sketch, "E8.36.8.1", {"start": v(1876.43, 3101.97) * mm, "end": v(1876.43, 3254.37) * mm});
            skLineSegment(sketch, "E8.39.8.1", {"start": v(2028.83, 3867.15) * mm, "end": v(1876.43, 3867.15) * mm});
            skLineSegment(sketch, "E8.42.8.1", {"start": v(2641.6, 3257.55) * mm, "end": v(2641.6, 3409.95) * mm});
            skLineSegment(sketch, "E8.45.8.1", {"start": v(1876.43, 3254.37) * mm, "end": v(2486.03, 3254.37) * mm});
            skLineSegment(sketch, "E8.0.8.2", {"start": v(1263.65, 3714.75) * mm, "end": v(1873.25, 3714.75) * mm});
            skLineSegment(sketch, "E8.3.8.2", {"start": v(1416.05, 3870.32) * mm, "end": v(1263.65, 3870.32) * mm});
            skLineSegment(sketch, "E8.6.8.2", {"start": v(1419.22, 3870.32) * mm, "end": v(1419.22, 4022.72) * mm});
            skLineSegment(sketch, "E8.9.8.2", {"start": v(1571.62, 4025.9) * mm, "end": v(1419.22, 4025.9) * mm});
            skLineSegment(sketch, "E8.12.8.2", {"start": v(1419.22, 3870.32) * mm, "end": v(2028.82, 3870.32) * mm});
            skLineSegment(sketch, "E8.15.8.2", {"start": v(1416.05, 3870.32) * mm, "end": v(1416.05, 4479.92) * mm});
            skLineSegment(sketch, "E8.18.8.2", {"start": v(1419.22, 4022.72) * mm, "end": v(2028.82, 4022.72) * mm});
            skLineSegment(sketch, "E8.21.8.2", {"start": v(1571.62, 4635.5) * mm, "end": v(1419.22, 4635.5) * mm});
            skLineSegment(sketch, "E8.24.8.2", {"start": v(1263.65, 3870.32) * mm, "end": v(1263.65, 4479.92) * mm});
            skLineSegment(sketch, "E8.27.8.2", {"start": v(1419.22, 4025.9) * mm, "end": v(1419.22, 4635.5) * mm});
            skLineSegment(sketch, "E8.30.8.2", {"start": v(1873.25, 3714.75) * mm, "end": v(1873.25, 3867.15) * mm});
            skLineSegment(sketch, "E8.33.8.2", {"start": v(1571.62, 4025.9) * mm, "end": v(1571.62, 4635.5) * mm});
            skLineSegment(sketch, "E8.36.8.2", {"start": v(1263.65, 3714.75) * mm, "end": v(1263.65, 3867.15) * mm});
            skLineSegment(sketch, "E8.39.8.2", {"start": v(1416.05, 4479.92) * mm, "end": v(1263.65, 4479.92) * mm});
            skLineSegment(sketch, "E8.42.8.2", {"start": v(2028.82, 3870.32) * mm, "end": v(2028.82, 4022.72) * mm});
            skLineSegment(sketch, "E8.45.8.2", {"start": v(1263.65, 3867.15) * mm, "end": v(1873.25, 3867.15) * mm});
            skLineSegment(sketch, "E8.0.8.3", {"start": v(650.87, 4327.52) * mm, "end": v(1260.47, 4327.52) * mm});
            skLineSegment(sketch, "E8.3.8.3", {"start": v(803.27, 4483.1) * mm, "end": v(650.87, 4483.1) * mm});
            skLineSegment(sketch, "E8.6.8.3", {"start": v(806.45, 4483.1) * mm, "end": v(806.45, 4635.5) * mm});
            skLineSegment(sketch, "E8.9.8.3", {"start": v(958.85, 4638.67) * mm, "end": v(806.45, 4638.67) * mm});
            skLineSegment(sketch, "E8.12.8.3", {"start": v(806.45, 4483.1) * mm, "end": v(1416.05, 4483.1) * mm});
            skLineSegment(sketch, "E8.15.8.3", {"start": v(803.27, 4483.1) * mm, "end": v(803.27, 5092.7) * mm});
            skLineSegment(sketch, "E8.18.8.3", {"start": v(806.45, 4635.5) * mm, "end": v(1416.05, 4635.5) * mm});
            skLineSegment(sketch, "E8.21.8.3", {"start": v(958.85, 5248.27) * mm, "end": v(806.45, 5248.27) * mm});
            skLineSegment(sketch, "E8.24.8.3", {"start": v(650.87, 4483.1) * mm, "end": v(650.87, 5092.7) * mm});
            skLineSegment(sketch, "E8.27.8.3", {"start": v(806.45, 4638.67) * mm, "end": v(806.45, 5248.27) * mm});
            skLineSegment(sketch, "E8.30.8.3", {"start": v(1260.47, 4327.52) * mm, "end": v(1260.47, 4479.92) * mm});
            skLineSegment(sketch, "E8.33.8.3", {"start": v(958.85, 4638.67) * mm, "end": v(958.85, 5248.27) * mm});
            skLineSegment(sketch, "E8.36.8.3", {"start": v(650.87, 4327.52) * mm, "end": v(650.87, 4479.92) * mm});
            skLineSegment(sketch, "E8.39.8.3", {"start": v(803.27, 5092.7) * mm, "end": v(650.87, 5092.7) * mm});
            skLineSegment(sketch, "E8.42.8.3", {"start": v(1416.05, 4483.1) * mm, "end": v(1416.05, 4635.5) * mm});
            skLineSegment(sketch, "E8.45.8.3", {"start": v(650.87, 4479.92) * mm, "end": v(1260.47, 4479.92) * mm});
            skLineSegment(sketch, "E8.0.8.4", {"start": v(38.1, 4940.3) * mm, "end": v(647.7, 4940.3) * mm});
            skLineSegment(sketch, "E8.3.8.4", {"start": v(190.5, 5095.87) * mm, "end": v(38.1, 5095.87) * mm});
            skLineSegment(sketch, "E8.6.8.4", {"start": v(193.67, 5095.87) * mm, "end": v(193.67, 5248.27) * mm});
            skLineSegment(sketch, "E8.9.8.4", {"start": v(346.07, 5251.45) * mm, "end": v(193.67, 5251.45) * mm});
            skLineSegment(sketch, "E8.12.8.4", {"start": v(193.67, 5095.87) * mm, "end": v(803.27, 5095.87) * mm});
            skLineSegment(sketch, "E8.15.8.4", {"start": v(190.5, 5095.87) * mm, "end": v(190.5, 5705.47) * mm});
            skLineSegment(sketch, "E8.18.8.4", {"start": v(193.67, 5248.27) * mm, "end": v(803.27, 5248.27) * mm});
            skLineSegment(sketch, "E8.21.8.4", {"start": v(346.07, 5861.05) * mm, "end": v(193.67, 5861.05) * mm});
            skLineSegment(sketch, "E8.24.8.4", {"start": v(38.1, 5095.87) * mm, "end": v(38.1, 5705.47) * mm});
            skLineSegment(sketch, "E8.27.8.4", {"start": v(193.67, 5251.45) * mm, "end": v(193.67, 5861.05) * mm});
            skLineSegment(sketch, "E8.30.8.4", {"start": v(647.7, 4940.3) * mm, "end": v(647.7, 5092.7) * mm});
            skLineSegment(sketch, "E8.33.8.4", {"start": v(346.07, 5251.45) * mm, "end": v(346.07, 5861.05) * mm});
            skLineSegment(sketch, "E8.36.8.4", {"start": v(38.1, 4940.3) * mm, "end": v(38.1, 5092.7) * mm});
            skLineSegment(sketch, "E8.39.8.4", {"start": v(190.5, 5705.47) * mm, "end": v(38.1, 5705.47) * mm});
            skLineSegment(sketch, "E8.42.8.4", {"start": v(803.27, 5095.87) * mm, "end": v(803.27, 5248.27) * mm});
            skLineSegment(sketch, "E8.45.8.4", {"start": v(38.1, 5092.7) * mm, "end": v(647.7, 5092.7) * mm});
            skSolve(sketch);
        }
        {
            var Q0;
            Q0=qSketchRegion(id+"F0",true);
            extrude(context, id + "F1", {"entities" : qUnion([Q0]), "depth" : 6.35 * mm, "offsetDistance" : 25.4 * mm});
        }
        {
            var Q0;
            Q0=qCreatedBy(makeId("Top.planeOp"),FACE);
            var sketch = newSketch(context, id + "F2", { "sketchPlane" : qUnion([Q0])});
            skLineSegment(sketch, "E9", {"start": v(1403.65, 2830.87) * mm, "end": v(303.57, 3930.95) * mm});
            skLineSegment(sketch, "E10", {"start": v(303.57, 3930.95) * mm, "end": v(-985.1, 2642.29) * mm});
            skLineSegment(sketch, "E11", {"start": v(-985.1, 2642.29) * mm, "end": v(114.99, 1542.2) * mm});
            skLineSegment(sketch, "E12", {"start": v(114.99, 1542.2) * mm, "end": v(1403.65, 2830.87) * mm});
            skLineSegment(sketch, "E13.bottom", {"start": v(-4816.06, 8587.4) * mm, "end": v(6787.9, 8587.4) * mm});
            skLineSegment(sketch, "E13.top", {"start": v(-4816.06, -1489.72) * mm, "end": v(6787.9, -1489.72) * mm});
            skLineSegment(sketch, "E13.left", {"start": v(-4816.06, 8587.4) * mm, "end": v(-4816.06, -1489.72) * mm});
            skLineSegment(sketch, "E13.right", {"start": v(6787.9, 8587.4) * mm, "end": v(6787.9, -1489.72) * mm});
            skLineSegment(sketch, "E14", {"start": v(952.5, 3403.6) * mm, "end": v(799.16, 3250.26) * mm, "construction": true});
            skLineSegment(sketch, "E15", {"start": v(796.93, 3400.42) * mm, "end": v(641.35, 3244.85) * mm, "construction": true});
            skLineSegment(sketch, "E16", {"start": v(774.6, 3378.1) * mm, "end": v(850.8, 3301.9) * mm, "construction": true});
            skLineSegment(sketch, "E17", {"start": v(853.61, 3380.91) * mm, "end": v(812.7, 3340) * mm, "construction": true});
            skSolve(sketch);
        }
        {
            var Q0;
            Q0=qSketchRegion(id+"F2",true);
            extrude(context, id + "F3", {"entities" : qUnion([Q0]), "operationType" : NewBodyOperationType.REMOVE, "endBound" : BoundingType.THROUGH_ALL, "depth" : 25.4 * mm, "offsetDistance" : 25.4 * mm});
        }
        {
            var Q0;
            Q0=makeQuery(id+"F1.opExtrude","SWEPT_BODY",BODY,{"disambiguationData":[OSD([sQuery(id+"F0.wireOp",EDGE,"E4.2.1.1"),sQuery(id+"F0.wireOp",EDGE,"E4.2.1.5"),sQuery(id+"F0.wireOp",EDGE,"E4.2.1.8"),sQuery(id+"F0.wireOp",EDGE,"E4.2.1.13")])]});
            var Q1;
            Q1=makeQuery(id+"F1.opExtrude","SWEPT_BODY",BODY,{"disambiguationData":[OSD([sQuery(id+"F0.wireOp",EDGE,"E4.2.1.3"),sQuery(id+"F0.wireOp",EDGE,"E4.2.1.7"),sQuery(id+"F0.wireOp",EDGE,"E4.2.1.9"),sQuery(id+"F0.wireOp",EDGE,"E4.2.1.11")])]});
            var Q2;
            Q2=makeQuery(id+"F1.opExtrude","SWEPT_BODY",BODY,{"disambiguationData":[OSD([sQuery(id+"F0.wireOp",EDGE,"E5.3.3.1"),sQuery(id+"F0.wireOp",EDGE,"E5.15.3.1"),sQuery(id+"F0.wireOp",EDGE,"E5.24.3.1"),sQuery(id+"F0.wireOp",EDGE,"E5.39.3.1")])]});
            var Q3;
            Q3=makeQuery(id+"F1.opExtrude","SWEPT_BODY",BODY,{"disambiguationData":[OSD([sQuery(id+"F0.wireOp",EDGE,"E5.9.3.1"),sQuery(id+"F0.wireOp",EDGE,"E5.21.3.1"),sQuery(id+"F0.wireOp",EDGE,"E5.27.3.1"),sQuery(id+"F0.wireOp",EDGE,"E5.33.3.1")])]});
            var Q4;
            Q4=makeQuery(id+"F1.opExtrude","SWEPT_BODY",BODY,{"disambiguationData":[OSD([sQuery(id+"F0.wireOp",EDGE,"E5.3.4.1"),sQuery(id+"F0.wireOp",EDGE,"E5.15.4.1"),sQuery(id+"F0.wireOp",EDGE,"E5.24.4.1"),sQuery(id+"F0.wireOp",EDGE,"E5.39.4.1")])]});
            var Q5;
            Q5=makeQuery(id+"F1.opExtrude","SWEPT_BODY",BODY,{"disambiguationData":[OSD([sQuery(id+"F0.wireOp",EDGE,"E5.9.4.1"),sQuery(id+"F0.wireOp",EDGE,"E5.21.4.1"),sQuery(id+"F0.wireOp",EDGE,"E5.27.4.1"),sQuery(id+"F0.wireOp",EDGE,"E5.33.4.1")])]});
            var Q6;
            Q6=makeQuery(id+"F1.opExtrude","SWEPT_BODY",BODY,{"disambiguationData":[OSD([sQuery(id+"F0.wireOp",EDGE,"E5.3.5.1"),sQuery(id+"F0.wireOp",EDGE,"E5.15.5.1"),sQuery(id+"F0.wireOp",EDGE,"E5.24.5.1"),sQuery(id+"F0.wireOp",EDGE,"E5.39.5.1")])]});
            var Q7;
            Q7=makeQuery(id+"F1.opExtrude","SWEPT_BODY",BODY,{"disambiguationData":[OSD([sQuery(id+"F0.wireOp",EDGE,"E5.9.5.1"),sQuery(id+"F0.wireOp",EDGE,"E5.21.5.1"),sQuery(id+"F0.wireOp",EDGE,"E5.27.5.1"),sQuery(id+"F0.wireOp",EDGE,"E5.33.5.1")])]});
            var Q8;
            Q8=makeQuery(id+"F1.opExtrude","SWEPT_BODY",BODY,{"disambiguationData":[OSD([sQuery(id+"F0.wireOp",EDGE,"E6.0.2.2"),sQuery(id+"F0.wireOp",EDGE,"E6.30.2.2"),sQuery(id+"F0.wireOp",EDGE,"E6.36.2.2"),sQuery(id+"F0.wireOp",EDGE,"E6.45.2.2")])]});
            var Q9;
            Q9=makeQuery(id+"F1.opExtrude","SWEPT_BODY",BODY,{"disambiguationData":[OSD([sQuery(id+"F0.wireOp",EDGE,"E6.3.2.2"),sQuery(id+"F0.wireOp",EDGE,"E6.15.2.2"),sQuery(id+"F0.wireOp",EDGE,"E6.24.2.2"),sQuery(id+"F0.wireOp",EDGE,"E6.39.2.2")])]});
            var Q10;
            Q10=makeQuery(id+"F1.opExtrude","SWEPT_BODY",BODY,{"disambiguationData":[OSD([sQuery(id+"F0.wireOp",EDGE,"E6.6.2.2"),sQuery(id+"F0.wireOp",EDGE,"E6.12.2.2"),sQuery(id+"F0.wireOp",EDGE,"E6.18.2.2"),sQuery(id+"F0.wireOp",EDGE,"E6.42.2.2")])]});
            var Q11;
            Q11=makeQuery(id+"F1.opExtrude","SWEPT_BODY",BODY,{"disambiguationData":[OSD([sQuery(id+"F0.wireOp",EDGE,"E6.9.2.2"),sQuery(id+"F0.wireOp",EDGE,"E6.21.2.2"),sQuery(id+"F0.wireOp",EDGE,"E6.27.2.2"),sQuery(id+"F0.wireOp",EDGE,"E6.33.2.2")])]});
            var Q12;
            Q12=makeQuery(id+"F1.opExtrude","SWEPT_BODY",BODY,{"disambiguationData":[OSD([sQuery(id+"F0.wireOp",EDGE,"E6.0.2.3"),sQuery(id+"F0.wireOp",EDGE,"E6.30.2.3"),sQuery(id+"F0.wireOp",EDGE,"E6.36.2.3"),sQuery(id+"F0.wireOp",EDGE,"E6.45.2.3")])]});
            var Q13;
            Q13=makeQuery(id+"F1.opExtrude","SWEPT_BODY",BODY,{"disambiguationData":[OSD([sQuery(id+"F0.wireOp",EDGE,"E6.6.2.3"),sQuery(id+"F0.wireOp",EDGE,"E6.12.2.3"),sQuery(id+"F0.wireOp",EDGE,"E6.18.2.3"),sQuery(id+"F0.wireOp",EDGE,"E6.42.2.3")])]});
            var Q14;
            Q14=makeQuery(id+"F1.opExtrude","SWEPT_BODY",BODY,{"disambiguationData":[OSD([sQuery(id+"F0.wireOp",EDGE,"E6.0.3.2"),sQuery(id+"F0.wireOp",EDGE,"E6.30.3.2"),sQuery(id+"F0.wireOp",EDGE,"E6.36.3.2"),sQuery(id+"F0.wireOp",EDGE,"E6.45.3.2")])]});
            var Q15;
            Q15=makeQuery(id+"F1.opExtrude","SWEPT_BODY",BODY,{"disambiguationData":[OSD([sQuery(id+"F0.wireOp",EDGE,"E6.3.3.2"),sQuery(id+"F0.wireOp",EDGE,"E6.15.3.2"),sQuery(id+"F0.wireOp",EDGE,"E6.24.3.2"),sQuery(id+"F0.wireOp",EDGE,"E6.39.3.2")])]});
            var Q16;
            Q16=makeQuery(id+"F1.opExtrude","SWEPT_BODY",BODY,{"disambiguationData":[OSD([sQuery(id+"F0.wireOp",EDGE,"E6.6.3.2"),sQuery(id+"F0.wireOp",EDGE,"E6.12.3.2"),sQuery(id+"F0.wireOp",EDGE,"E6.18.3.2"),sQuery(id+"F0.wireOp",EDGE,"E6.42.3.2")])]});
            var Q17;
            Q17=makeQuery(id+"F1.opExtrude","SWEPT_BODY",BODY,{"disambiguationData":[OSD([sQuery(id+"F0.wireOp",EDGE,"E6.9.3.2"),sQuery(id+"F0.wireOp",EDGE,"E6.21.3.2"),sQuery(id+"F0.wireOp",EDGE,"E6.27.3.2"),sQuery(id+"F0.wireOp",EDGE,"E6.33.3.2")])]});
            var Q18;
            Q18=makeQuery(id+"F1.opExtrude","SWEPT_BODY",BODY,{"disambiguationData":[OSD([sQuery(id+"F0.wireOp",EDGE,"E6.0.3.3"),sQuery(id+"F0.wireOp",EDGE,"E6.30.3.3"),sQuery(id+"F0.wireOp",EDGE,"E6.36.3.3"),sQuery(id+"F0.wireOp",EDGE,"E6.45.3.3")])]});
            var Q19;
            Q19=makeQuery(id+"F1.opExtrude","SWEPT_BODY",BODY,{"disambiguationData":[OSD([sQuery(id+"F0.wireOp",EDGE,"E6.6.3.3"),sQuery(id+"F0.wireOp",EDGE,"E6.12.3.3"),sQuery(id+"F0.wireOp",EDGE,"E6.18.3.3"),sQuery(id+"F0.wireOp",EDGE,"E6.42.3.3")])]});
            var Q20;
            Q20=makeQuery(id+"F1.opExtrude","SWEPT_BODY",BODY,{"disambiguationData":[OSD([sQuery(id+"F0.wireOp",EDGE,"E6.0.4.2"),sQuery(id+"F0.wireOp",EDGE,"E6.30.4.2"),sQuery(id+"F0.wireOp",EDGE,"E6.36.4.2"),sQuery(id+"F0.wireOp",EDGE,"E6.45.4.2")])]});
            var Q21;
            Q21=makeQuery(id+"F1.opExtrude","SWEPT_BODY",BODY,{"disambiguationData":[OSD([sQuery(id+"F0.wireOp",EDGE,"E6.3.4.2"),sQuery(id+"F0.wireOp",EDGE,"E6.15.4.2"),sQuery(id+"F0.wireOp",EDGE,"E6.24.4.2"),sQuery(id+"F0.wireOp",EDGE,"E6.39.4.2")])]});
            var Q22;
            Q22=makeQuery(id+"F1.opExtrude","SWEPT_BODY",BODY,{"disambiguationData":[OSD([sQuery(id+"F0.wireOp",EDGE,"E6.6.4.2"),sQuery(id+"F0.wireOp",EDGE,"E6.12.4.2"),sQuery(id+"F0.wireOp",EDGE,"E6.18.4.2"),sQuery(id+"F0.wireOp",EDGE,"E6.42.4.2")])]});
            var Q23;
            Q23=makeQuery(id+"F1.opExtrude","SWEPT_BODY",BODY,{"disambiguationData":[OSD([sQuery(id+"F0.wireOp",EDGE,"E6.9.4.2"),sQuery(id+"F0.wireOp",EDGE,"E6.21.4.2"),sQuery(id+"F0.wireOp",EDGE,"E6.27.4.2"),sQuery(id+"F0.wireOp",EDGE,"E6.33.4.2")])]});
            var Q24;
            Q24=makeQuery(id+"F1.opExtrude","SWEPT_BODY",BODY,{"disambiguationData":[OSD([sQuery(id+"F0.wireOp",EDGE,"E6.0.4.3"),sQuery(id+"F0.wireOp",EDGE,"E6.30.4.3"),sQuery(id+"F0.wireOp",EDGE,"E6.36.4.3"),sQuery(id+"F0.wireOp",EDGE,"E6.45.4.3")])]});
            var Q25;
            Q25=makeQuery(id+"F1.opExtrude","SWEPT_BODY",BODY,{"disambiguationData":[OSD([sQuery(id+"F0.wireOp",EDGE,"E6.6.4.3"),sQuery(id+"F0.wireOp",EDGE,"E6.12.4.3"),sQuery(id+"F0.wireOp",EDGE,"E6.18.4.3"),sQuery(id+"F0.wireOp",EDGE,"E6.42.4.3")])]});
            var Q26;
            Q26=makeQuery(id+"F1.opExtrude","SWEPT_BODY",BODY,{"disambiguationData":[OSD([sQuery(id+"F0.wireOp",EDGE,"E6.0.5.2"),sQuery(id+"F0.wireOp",EDGE,"E6.30.5.2"),sQuery(id+"F0.wireOp",EDGE,"E6.36.5.2"),sQuery(id+"F0.wireOp",EDGE,"E6.45.5.2")])]});
            var Q27;
            Q27=makeQuery(id+"F1.opExtrude","SWEPT_BODY",BODY,{"disambiguationData":[OSD([sQuery(id+"F0.wireOp",EDGE,"E6.3.5.2"),sQuery(id+"F0.wireOp",EDGE,"E6.15.5.2"),sQuery(id+"F0.wireOp",EDGE,"E6.24.5.2"),sQuery(id+"F0.wireOp",EDGE,"E6.39.5.2")])]});
            var Q28;
            Q28=makeQuery(id+"F1.opExtrude","SWEPT_BODY",BODY,{"disambiguationData":[OSD([sQuery(id+"F0.wireOp",EDGE,"E6.6.5.2"),sQuery(id+"F0.wireOp",EDGE,"E6.12.5.2"),sQuery(id+"F0.wireOp",EDGE,"E6.18.5.2"),sQuery(id+"F0.wireOp",EDGE,"E6.42.5.2")])]});
            var Q29;
            Q29=makeQuery(id+"F1.opExtrude","SWEPT_BODY",BODY,{"disambiguationData":[OSD([sQuery(id+"F0.wireOp",EDGE,"E6.9.5.2"),sQuery(id+"F0.wireOp",EDGE,"E6.21.5.2"),sQuery(id+"F0.wireOp",EDGE,"E6.27.5.2"),sQuery(id+"F0.wireOp",EDGE,"E6.33.5.2")])]});
            var Q30;
            Q30=makeQuery(id+"F1.opExtrude","SWEPT_BODY",BODY,{"disambiguationData":[OSD([sQuery(id+"F0.wireOp",EDGE,"E6.0.5.3"),sQuery(id+"F0.wireOp",EDGE,"E6.30.5.3"),sQuery(id+"F0.wireOp",EDGE,"E6.36.5.3"),sQuery(id+"F0.wireOp",EDGE,"E6.45.5.3")])]});
            var Q31;
            Q31=makeQuery(id+"F1.opExtrude","SWEPT_BODY",BODY,{"disambiguationData":[OSD([sQuery(id+"F0.wireOp",EDGE,"E6.6.5.3"),sQuery(id+"F0.wireOp",EDGE,"E6.12.5.3"),sQuery(id+"F0.wireOp",EDGE,"E6.18.5.3"),sQuery(id+"F0.wireOp",EDGE,"E6.42.5.3")])]});
            var Q32;
            Q32=makeQuery(id+"F1.opExtrude","SWEPT_BODY",BODY,{"disambiguationData":[OSD([sQuery(id+"F0.wireOp",EDGE,"E7.3.6.1"),sQuery(id+"F0.wireOp",EDGE,"E7.15.6.1"),sQuery(id+"F0.wireOp",EDGE,"E7.24.6.1"),sQuery(id+"F0.wireOp",EDGE,"E7.39.6.1")])]});
            var Q33;
            Q33=makeQuery(id+"F1.opExtrude","SWEPT_BODY",BODY,{"disambiguationData":[OSD([sQuery(id+"F0.wireOp",EDGE,"E7.0.6.2"),sQuery(id+"F0.wireOp",EDGE,"E7.30.6.2"),sQuery(id+"F0.wireOp",EDGE,"E7.36.6.2"),sQuery(id+"F0.wireOp",EDGE,"E7.45.6.2")])]});
            var Q34;
            Q34=makeQuery(id+"F1.opExtrude","SWEPT_BODY",BODY,{"disambiguationData":[OSD([sQuery(id+"F0.wireOp",EDGE,"E7.3.6.2"),sQuery(id+"F0.wireOp",EDGE,"E7.15.6.2"),sQuery(id+"F0.wireOp",EDGE,"E7.24.6.2"),sQuery(id+"F0.wireOp",EDGE,"E7.39.6.2")])]});
            var Q35;
            Q35=makeQuery(id+"F1.opExtrude","SWEPT_BODY",BODY,{"disambiguationData":[OSD([sQuery(id+"F0.wireOp",EDGE,"E7.6.6.2"),sQuery(id+"F0.wireOp",EDGE,"E7.12.6.2"),sQuery(id+"F0.wireOp",EDGE,"E7.18.6.2"),sQuery(id+"F0.wireOp",EDGE,"E7.42.6.2")])]});
            var Q36;
            Q36=makeQuery(id+"F1.opExtrude","SWEPT_BODY",BODY,{"disambiguationData":[OSD([sQuery(id+"F0.wireOp",EDGE,"E7.9.6.2"),sQuery(id+"F0.wireOp",EDGE,"E7.21.6.2"),sQuery(id+"F0.wireOp",EDGE,"E7.27.6.2"),sQuery(id+"F0.wireOp",EDGE,"E7.33.6.2")])]});
            var Q37;
            Q37=makeQuery(id+"F1.opExtrude","SWEPT_BODY",BODY,{"disambiguationData":[OSD([sQuery(id+"F0.wireOp",EDGE,"E7.0.6.3"),sQuery(id+"F0.wireOp",EDGE,"E7.30.6.3"),sQuery(id+"F0.wireOp",EDGE,"E7.36.6.3"),sQuery(id+"F0.wireOp",EDGE,"E7.45.6.3")])]});
            var Q38;
            Q38=makeQuery(id+"F1.opExtrude","SWEPT_BODY",BODY,{"disambiguationData":[OSD([sQuery(id+"F0.wireOp",EDGE,"E7.6.6.3"),sQuery(id+"F0.wireOp",EDGE,"E7.12.6.3"),sQuery(id+"F0.wireOp",EDGE,"E7.18.6.3"),sQuery(id+"F0.wireOp",EDGE,"E7.42.6.3")])]});
            var Q39;
            Q39=makeQuery(id+"F1.opExtrude","SWEPT_BODY",BODY,{"disambiguationData":[OSD([sQuery(id+"F0.wireOp",EDGE,"E4.1.1.3"),sQuery(id+"F0.wireOp",EDGE,"E4.1.1.7"),sQuery(id+"F0.wireOp",EDGE,"E4.1.1.9"),sQuery(id+"F0.wireOp",EDGE,"E4.1.1.11")])]});
            var Q40;
            Q40=makeQuery(id+"F1.opExtrude","SWEPT_BODY",BODY,{"disambiguationData":[OSD([sQuery(id+"F0.wireOp",EDGE,"E6.6.1.2"),sQuery(id+"F0.wireOp",EDGE,"E6.12.1.2"),sQuery(id+"F0.wireOp",EDGE,"E6.18.1.2"),sQuery(id+"F0.wireOp",EDGE,"E6.42.1.2")])]});
            var Q41;
            Q41=makeQuery(id+"F1.opExtrude","SWEPT_BODY",BODY,{"disambiguationData":[OSD([sQuery(id+"F0.wireOp",EDGE,"E6.9.1.2"),sQuery(id+"F0.wireOp",EDGE,"E6.21.1.2"),sQuery(id+"F0.wireOp",EDGE,"E6.27.1.2"),sQuery(id+"F0.wireOp",EDGE,"E6.33.1.2")])]});
            var Q42;
            Q42=makeQuery(id+"F1.opExtrude","SWEPT_BODY",BODY,{"disambiguationData":[OSD([sQuery(id+"F0.wireOp",EDGE,"E6.6.1.3"),sQuery(id+"F0.wireOp",EDGE,"E6.12.1.3"),sQuery(id+"F0.wireOp",EDGE,"E6.18.1.3"),sQuery(id+"F0.wireOp",EDGE,"E6.42.1.3")])]});
            var Q43;
            Q43=makeQuery(id+"F3.boolean.opBoolean","COPY",EDGE,{"derivedFrom":makeQuery(id+"F3.opExtrude","SWEPT_EDGE",EDGE,{"disambiguationData":[OSD([sQuery(id+"F2.wireOp",EDGE,"E10"),sQuery(id+"F2.wireOp",EDGE,"E11")])]})});
            transform(context, id + "F4", {"entities" : qUnion([Q0, Q1, Q2, Q3, Q4, Q5, Q6, Q7, Q8, Q9, Q10, Q11, Q12, Q13, Q14, Q15, Q16, Q17, Q18, Q19, Q20, Q21, Q22, Q23, Q24, Q25, Q26, Q27, Q28, Q29, Q30, Q31, Q32, Q33, Q34, Q35, Q36, Q37, Q38, Q39, Q40, Q41, Q42]), "transformType" : TransformType.ROTATION, "transformAxis" : qUnion([Q43]), "angle" : 135 * degree, "oppositeDirection" : true, "makeCopy" : false});
        }
    });
